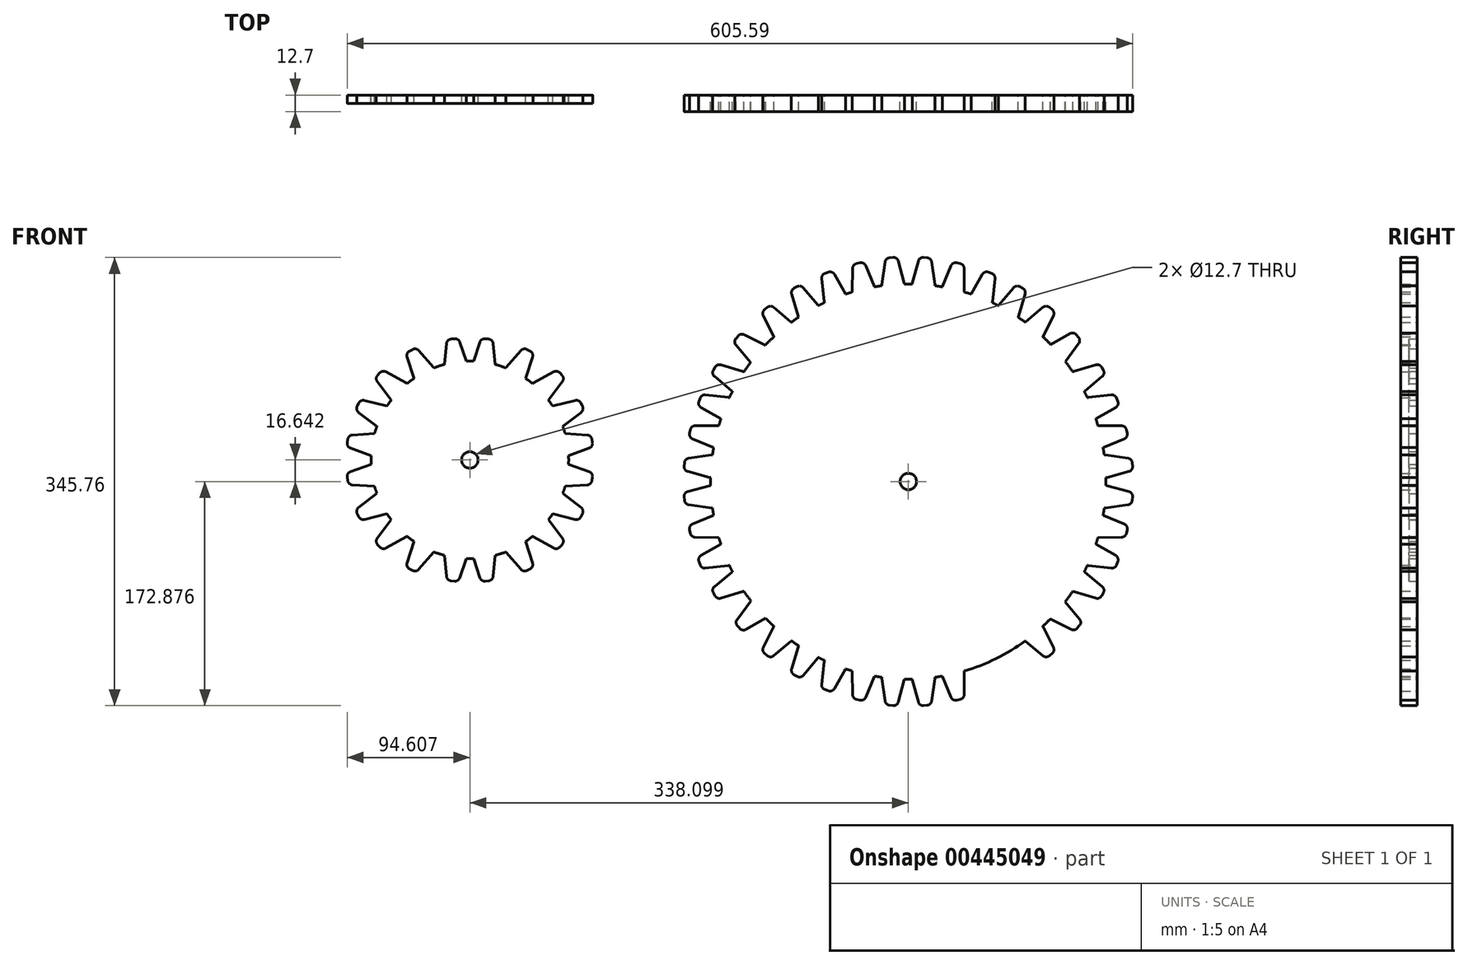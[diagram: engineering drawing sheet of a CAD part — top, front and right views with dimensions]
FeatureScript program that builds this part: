
annotation { "Feature Type Name" : "Feature", "Feature Type Description" : "" }
export const myFeature = defineFeature(function(context is Context, id is Id, definition is map)
    precondition{}
    {
        {
            var Q0;
            Q0=qCreatedBy(makeId("Front.planeOp"),FACE);
            var sketch = newSketch(context, id + "F0", { "sketchPlane" : qUnion([Q0])});
            skCircle(sketch, "E0", {"center": v(90.4, 32.98) * mm, "radius": 152.4 * mm});
            skCircle(sketch, "E1", {"center": v(90.4, 32.98) * mm, "radius": 6.35 * mm});
            skCircle(sketch, "E2", {"center": v(-294.65, -11.85) * mm, "radius": 76.2 * mm});
            skCircle(sketch, "E3", {"center": v(-294.65, -11.85) * mm, "radius": 6.35 * mm});
            skLineSegment(sketch, "E4", {"start": v(-82.46, 44.7) * mm, "end": v(-82.22, 47.48) * mm});
            skLineSegment(sketch, "E5", {"start": v(-78.98, 50.92) * mm, "end": v(-61.5, 53.51) * mm});
            skLineSegment(sketch, "E6", {"start": v(-57.15, 49.41) * mm, "end": v(-58.01, 39.52) * mm});
            skLineSegment(sketch, "E7", {"start": v(-62.8, 36.17) * mm, "end": v(-79.65, 40.7) * mm});
            skPoint(sketch, "E8.visualSharp", {"position": v(-82.74, 41.52) * mm});
            skArc(sketch, "E8.filletArc", {"start": v(-82.46, 44.7) * mm, "mid": v(-81.78, 42.19) * mm, "end": v(-79.65, 40.7) * mm});
            skPoint(sketch, "E9.visualSharp", {"position": v(-81.95, 50.47) * mm});
            skArc(sketch, "E9.filletArc", {"start": v(-78.98, 50.92) * mm, "mid": v(-81.2, 49.76) * mm, "end": v(-82.22, 47.48) * mm});
            skArc(sketch, "E10.filletArc", {"start": v(-57.15, 49.41) * mm, "mid": v(-58.33, 52.52) * mm, "end": v(-61.5, 53.51) * mm});
            skArc(sketch, "E11.filletArc", {"start": v(-62.8, 36.17) * mm, "mid": v(-59.62, 36.73) * mm, "end": v(-58.01, 39.52) * mm});
            skLineSegment(sketch, "E12", {"start": v(-71.1, 94.66) * mm, "end": v(-70.15, 97.29) * mm});
            skLineSegment(sketch, "E13", {"start": v(-66.15, 99.78) * mm, "end": v(-48.58, 97.84) * mm});
            skLineSegment(sketch, "E14", {"start": v(-45.42, 92.76) * mm, "end": v(-48.78, 83.42) * mm});
            skLineSegment(sketch, "E15", {"start": v(-54.25, 81.4) * mm, "end": v(-69.4, 90.07) * mm});
            skPoint(sketch, "E16.visualSharp", {"position": v(-72.18, 91.66) * mm});
            skArc(sketch, "E16.filletArc", {"start": v(-71.1, 94.66) * mm, "mid": v(-71.09, 92.06) * mm, "end": v(-69.4, 90.07) * mm});
            skArc(sketch, "E17.filletArc", {"start": v(-66.15, 99.78) * mm, "mid": v(-68.58, 99.23) * mm, "end": v(-70.15, 97.29) * mm});
            skArc(sketch, "E18.filletArc", {"start": v(-45.42, 92.76) * mm, "mid": v(-45.77, 96.07) * mm, "end": v(-48.58, 97.84) * mm});
            skArc(sketch, "E19.filletArc", {"start": v(-54.25, 81.4) * mm, "mid": v(-51.05, 81.13) * mm, "end": v(-48.78, 83.42) * mm});
            skLineSegment(sketch, "E20", {"start": v(-59.95, 118.83) * mm, "end": v(-58.56, 121.24) * mm});
            skLineSegment(sketch, "E21", {"start": v(-54.17, 122.99) * mm, "end": v(-37.23, 117.95) * mm});
            skLineSegment(sketch, "E22", {"start": v(-35.02, 112.4) * mm, "end": v(-39.98, 103.8) * mm});
            skLineSegment(sketch, "E23", {"start": v(-45.73, 102.79) * mm, "end": v(-59.1, 114) * mm});
            skPoint(sketch, "E24.visualSharp", {"position": v(-61.55, 116.06) * mm});
            skArc(sketch, "E24.filletArc", {"start": v(-59.95, 118.83) * mm, "mid": v(-60.4, 116.26) * mm, "end": v(-59.1, 114) * mm});
            skPoint(sketch, "E25.visualSharp", {"position": v(-57.05, 123.84) * mm});
            skArc(sketch, "E25.filletArc", {"start": v(-54.17, 122.99) * mm, "mid": v(-56.67, 122.88) * mm, "end": v(-58.56, 121.24) * mm});
            skArc(sketch, "E26.filletArc", {"start": v(-35.02, 112.4) * mm, "mid": v(-34.78, 115.71) * mm, "end": v(-37.23, 117.95) * mm});
            skArc(sketch, "E27.filletArc", {"start": v(-45.73, 102.79) * mm, "mid": v(-42.62, 101.95) * mm, "end": v(-39.98, 103.8) * mm});
            skLineSegment(sketch, "E28", {"start": v(-78.33, 70.27) * mm, "end": v(-77.71, 72.99) * mm});
            skLineSegment(sketch, "E29", {"start": v(-74.04, 75.96) * mm, "end": v(-56.37, 76.18) * mm});
            skLineSegment(sketch, "E30", {"start": v(-52.61, 71.53) * mm, "end": v(-54.8, 61.85) * mm});
            skLineSegment(sketch, "E31", {"start": v(-59.99, 59.17) * mm, "end": v(-76.08, 65.92) * mm});
            skPoint(sketch, "E32.visualSharp", {"position": v(-79.03, 67.15) * mm});
            skArc(sketch, "E32.filletArc", {"start": v(-78.33, 70.27) * mm, "mid": v(-78, 67.68) * mm, "end": v(-76.08, 65.92) * mm});
            skPoint(sketch, "E33.visualSharp", {"position": v(-77.05, 75.92) * mm});
            skArc(sketch, "E33.filletArc", {"start": v(-74.04, 75.96) * mm, "mid": v(-76.4, 75.1) * mm, "end": v(-77.71, 72.99) * mm});
            skArc(sketch, "E34.filletArc", {"start": v(-52.61, 71.53) * mm, "mid": v(-53.37, 74.77) * mm, "end": v(-56.37, 76.18) * mm});
            skArc(sketch, "E35.filletArc", {"start": v(-59.99, 59.17) * mm, "mid": v(-56.77, 59.3) * mm, "end": v(-54.8, 61.85) * mm});
            skLineSegment(sketch, "E36.MirrorCS", {"start": v(-7.67, 143.95) * mm, "end": v(-0.07, 150.34) * mm});
            skLineSegment(sketch, "E37.MirrorCS", {"start": v(-0.07, 156.17) * mm, "end": v(-13.44, 167.4) * mm});
            skLineSegment(sketch, "E38.MirrorCS", {"start": v(-21.43, 160.98) * mm, "end": v(-13.53, 145.17) * mm});
            skPoint(sketch, "E39.MirrorP", {"position": v(-22.77, 163.67) * mm});
            skArc(sketch, "E40.MirrorCS", {"start": v(-21.43, 160.98) * mm, "mid": v(-21.75, 163.45) * mm, "end": v(-20.47, 165.6) * mm});
            skArc(sketch, "E41.MirrorCS", {"start": v(-18.33, 167.4) * mm, "mid": v(-15.88, 168.28) * mm, "end": v(-13.44, 167.4) * mm});
            skLineSegment(sketch, "E42.MirrorCS", {"start": v(-18.33, 167.4) * mm, "end": v(-20.47, 165.6) * mm});
            skArc(sketch, "E43.MirrorCS", {"start": v(-7.67, 143.95) * mm, "mid": v(-10.9, 143.14) * mm, "end": v(-13.53, 145.17) * mm});
            skArc(sketch, "E44.MirrorCS", {"start": v(-0.07, 156.17) * mm, "mid": v(1.3, 153.25) * mm, "end": v(-0.07, 150.34) * mm});
            skLineSegment(sketch, "E45.MirrorCS", {"start": v(10.98, 158.4) * mm, "end": v(19.58, 163.36) * mm});
            skArc(sketch, "E46.MirrorCS", {"start": v(10.98, 158.4) * mm, "mid": v(7.67, 158.16) * mm, "end": v(5.43, 160.61) * mm});
            skArc(sketch, "E47.MirrorCS", {"start": v(20.6, 169.11) * mm, "mid": v(21.43, 166) * mm, "end": v(19.58, 163.36) * mm});
            skLineSegment(sketch, "E48.MirrorCS", {"start": v(20.6, 169.11) * mm, "end": v(9.38, 182.48) * mm});
            skLineSegment(sketch, "E49.MirrorCS", {"start": v(0.4, 177.55) * mm, "end": v(5.43, 160.61) * mm});
            skPoint(sketch, "E50.MirrorP", {"position": v(-0.46, 180.43) * mm});
            skArc(sketch, "E51.MirrorCS", {"start": v(0.4, 177.55) * mm, "mid": v(0.5, 180.05) * mm, "end": v(2.14, 181.94) * mm});
            skLineSegment(sketch, "E52.MirrorCS", {"start": v(4.55, 183.33) * mm, "end": v(2.14, 181.94) * mm});
            skArc(sketch, "E53.MirrorCS", {"start": v(4.55, 183.33) * mm, "mid": v(7.12, 183.78) * mm, "end": v(9.38, 182.48) * mm});
            skArc(sketch, "E54.MirrorCS", {"start": v(30.62, 168.8) * mm, "mid": v(27.32, 169.15) * mm, "end": v(25.55, 171.97) * mm});
            skLineSegment(sketch, "E55.MirrorCS", {"start": v(30.62, 168.8) * mm, "end": v(39.96, 172.16) * mm});
            skArc(sketch, "E56.MirrorCS", {"start": v(41.98, 177.64) * mm, "mid": v(42.25, 174.43) * mm, "end": v(39.96, 172.16) * mm});
            skLineSegment(sketch, "E57.MirrorCS", {"start": v(41.98, 177.64) * mm, "end": v(33.31, 192.78) * mm});
            skLineSegment(sketch, "E58.MirrorCS", {"start": v(23.6, 189.53) * mm, "end": v(25.55, 171.97) * mm});
            skArc(sketch, "E59.MirrorCS", {"start": v(23.6, 189.53) * mm, "mid": v(24.15, 191.97) * mm, "end": v(26.1, 193.53) * mm});
            skLineSegment(sketch, "E60.MirrorCS", {"start": v(28.72, 194.48) * mm, "end": v(26.1, 193.53) * mm});
            skArc(sketch, "E61.MirrorCS", {"start": v(28.72, 194.48) * mm, "mid": v(31.32, 194.47) * mm, "end": v(33.31, 192.78) * mm});
            skLineSegment(sketch, "E62.MirrorCS", {"start": v(47.42, 197.43) * mm, "end": v(47.2, 179.76) * mm});
            skArc(sketch, "E63.MirrorCS", {"start": v(47.42, 197.43) * mm, "mid": v(48.27, 199.78) * mm, "end": v(50.4, 201.1) * mm});
            skLineSegment(sketch, "E64.MirrorCS", {"start": v(53.11, 201.7) * mm, "end": v(50.4, 201.1) * mm});
            skArc(sketch, "E65.MirrorCS", {"start": v(53.11, 201.7) * mm, "mid": v(55.7, 201.38) * mm, "end": v(57.47, 199.46) * mm});
            skLineSegment(sketch, "E66.MirrorCS", {"start": v(64.2, 183.37) * mm, "end": v(57.47, 199.46) * mm});
            skArc(sketch, "E67.MirrorCS", {"start": v(64.2, 183.37) * mm, "mid": v(64.08, 180.15) * mm, "end": v(61.53, 178.18) * mm});
            skLineSegment(sketch, "E68.MirrorCS", {"start": v(51.85, 176) * mm, "end": v(61.53, 178.18) * mm});
            skArc(sketch, "E69.MirrorCS", {"start": v(51.85, 176) * mm, "mid": v(48.61, 176.75) * mm, "end": v(47.2, 179.76) * mm});
            skArc(sketch, "E70.MirrorCS", {"start": v(73.97, 180.53) * mm, "mid": v(70.86, 181.71) * mm, "end": v(69.87, 184.88) * mm});
            skLineSegment(sketch, "E71.MirrorCS", {"start": v(73.97, 180.53) * mm, "end": v(83.86, 181.4) * mm});
            skArc(sketch, "E72.MirrorCS", {"start": v(87.2, 186.17) * mm, "mid": v(86.65, 183) * mm, "end": v(83.86, 181.4) * mm});
            skLineSegment(sketch, "E73.MirrorCS", {"start": v(87.2, 186.17) * mm, "end": v(82.69, 203.03) * mm});
            skArc(sketch, "E74.MirrorCS", {"start": v(78.68, 205.84) * mm, "mid": v(81.2, 205.17) * mm, "end": v(82.69, 203.03) * mm});
            skLineSegment(sketch, "E75.MirrorCS", {"start": v(78.68, 205.84) * mm, "end": v(75.9, 205.6) * mm});
            skArc(sketch, "E76.MirrorCS", {"start": v(72.47, 202.36) * mm, "mid": v(73.62, 204.58) * mm, "end": v(75.9, 205.6) * mm});
            skLineSegment(sketch, "E77.MirrorCS", {"start": v(72.47, 202.36) * mm, "end": v(69.87, 184.88) * mm});
            skLineSegment(sketch, "E78.MirrorCS", {"start": v(93.6, 186.17) * mm, "end": v(98.12, 203.03) * mm});
            skLineSegment(sketch, "E79.MirrorCS", {"start": v(108.35, 202.36) * mm, "end": v(110.94, 184.88) * mm});
            skArc(sketch, "E80.MirrorCS", {"start": v(106.84, 180.53) * mm, "mid": v(109.95, 181.71) * mm, "end": v(110.94, 184.88) * mm});
            skLineSegment(sketch, "E81.MirrorCS", {"start": v(106.84, 180.53) * mm, "end": v(96.95, 181.4) * mm});
            skArc(sketch, "E82.MirrorCS", {"start": v(93.6, 186.17) * mm, "mid": v(94.16, 183) * mm, "end": v(96.95, 181.4) * mm});
            skLineSegment(sketch, "E83.MirrorCS", {"start": v(102.13, 205.84) * mm, "end": v(104.9, 205.6) * mm});
            skArc(sketch, "E84.MirrorCS", {"start": v(108.35, 202.36) * mm, "mid": v(107.19, 204.58) * mm, "end": v(104.9, 205.6) * mm});
            skArc(sketch, "E85.MirrorCS", {"start": v(102.13, 205.84) * mm, "mid": v(99.62, 205.17) * mm, "end": v(98.12, 203.03) * mm});
            skArc(sketch, "E86.MirrorCS", {"start": v(127.7, 201.7) * mm, "mid": v(125.11, 201.38) * mm, "end": v(123.35, 199.46) * mm});
            skLineSegment(sketch, "E87.MirrorCS", {"start": v(127.7, 201.7) * mm, "end": v(130.42, 201.1) * mm});
            skArc(sketch, "E88.MirrorCS", {"start": v(133.39, 197.43) * mm, "mid": v(132.54, 199.78) * mm, "end": v(130.42, 201.1) * mm});
            skLineSegment(sketch, "E89.MirrorCS", {"start": v(133.39, 197.43) * mm, "end": v(133.6, 179.76) * mm});
            skArc(sketch, "E90.MirrorCS", {"start": v(128.96, 176) * mm, "mid": v(132.2, 176.75) * mm, "end": v(133.6, 179.76) * mm});
            skLineSegment(sketch, "E91.MirrorCS", {"start": v(128.96, 176) * mm, "end": v(119.28, 178.18) * mm});
            skArc(sketch, "E92.MirrorCS", {"start": v(116.6, 183.37) * mm, "mid": v(116.73, 180.15) * mm, "end": v(119.28, 178.18) * mm});
            skLineSegment(sketch, "E93.MirrorCS", {"start": v(116.6, 183.37) * mm, "end": v(123.35, 199.46) * mm});
            skLineSegment(sketch, "E94.MirrorCS", {"start": v(138.83, 177.64) * mm, "end": v(147.5, 192.78) * mm});
            skArc(sketch, "E95.MirrorCS", {"start": v(152.1, 194.48) * mm, "mid": v(149.49, 194.47) * mm, "end": v(147.5, 192.78) * mm});
            skLineSegment(sketch, "E96.MirrorCS", {"start": v(152.1, 194.48) * mm, "end": v(154.72, 193.53) * mm});
            skArc(sketch, "E97.MirrorCS", {"start": v(157.21, 189.53) * mm, "mid": v(156.66, 191.97) * mm, "end": v(154.72, 193.53) * mm});
            skLineSegment(sketch, "E98.MirrorCS", {"start": v(157.21, 189.53) * mm, "end": v(155.27, 171.97) * mm});
            skArc(sketch, "E99.MirrorCS", {"start": v(150.2, 168.8) * mm, "mid": v(153.5, 169.15) * mm, "end": v(155.27, 171.97) * mm});
            skLineSegment(sketch, "E100.MirrorCS", {"start": v(150.2, 168.8) * mm, "end": v(140.85, 172.16) * mm});
            skArc(sketch, "E101.MirrorCS", {"start": v(138.83, 177.64) * mm, "mid": v(138.56, 174.43) * mm, "end": v(140.85, 172.16) * mm});
            skLineSegment(sketch, "E102.MirrorCS", {"start": v(160.22, 169.11) * mm, "end": v(171.43, 182.48) * mm});
            skArc(sketch, "E103.MirrorCS", {"start": v(176.26, 183.33) * mm, "mid": v(173.7, 183.78) * mm, "end": v(171.43, 182.48) * mm});
            skLineSegment(sketch, "E104.MirrorCS", {"start": v(176.26, 183.33) * mm, "end": v(178.67, 181.94) * mm});
            skArc(sketch, "E105.MirrorCS", {"start": v(180.42, 177.55) * mm, "mid": v(180.3, 180.05) * mm, "end": v(178.67, 181.94) * mm});
            skLineSegment(sketch, "E106.MirrorCS", {"start": v(180.42, 177.55) * mm, "end": v(175.38, 160.61) * mm});
            skArc(sketch, "E107.MirrorCS", {"start": v(169.83, 158.4) * mm, "mid": v(173.14, 158.16) * mm, "end": v(175.38, 160.61) * mm});
            skLineSegment(sketch, "E108.MirrorCS", {"start": v(169.83, 158.4) * mm, "end": v(161.23, 163.36) * mm});
            skArc(sketch, "E109.MirrorCS", {"start": v(160.22, 169.11) * mm, "mid": v(159.38, 166) * mm, "end": v(161.23, 163.36) * mm});
            skArc(sketch, "E110.MirrorCS", {"start": v(180.88, 156.17) * mm, "mid": v(179.52, 153.25) * mm, "end": v(180.88, 150.34) * mm});
            skLineSegment(sketch, "E111.MirrorCS", {"start": v(180.88, 156.17) * mm, "end": v(194.25, 167.4) * mm});
            skArc(sketch, "E112.MirrorCS", {"start": v(199.15, 167.4) * mm, "mid": v(196.7, 168.28) * mm, "end": v(194.25, 167.4) * mm});
            skLineSegment(sketch, "E113.MirrorCS", {"start": v(199.15, 167.4) * mm, "end": v(201.28, 165.6) * mm});
            skArc(sketch, "E114.MirrorCS", {"start": v(202.24, 160.98) * mm, "mid": v(202.56, 163.45) * mm, "end": v(201.28, 165.6) * mm});
            skLineSegment(sketch, "E115.MirrorCS", {"start": v(202.24, 160.98) * mm, "end": v(194.34, 145.17) * mm});
            skArc(sketch, "E116.MirrorCS", {"start": v(188.48, 143.95) * mm, "mid": v(191.7, 143.14) * mm, "end": v(194.34, 145.17) * mm});
            skLineSegment(sketch, "E117.MirrorCS", {"start": v(188.48, 143.95) * mm, "end": v(180.88, 150.34) * mm});
            skLineSegment(sketch, "E118.MirrorCS", {"start": v(234.98, 122.99) * mm, "end": v(218.04, 117.95) * mm});
            skArc(sketch, "E119.MirrorCS", {"start": v(234.98, 122.99) * mm, "mid": v(237.48, 122.88) * mm, "end": v(239.37, 121.24) * mm});
            skLineSegment(sketch, "E120.MirrorCS", {"start": v(240.76, 118.83) * mm, "end": v(239.37, 121.24) * mm});
            skArc(sketch, "E121.MirrorCS", {"start": v(240.76, 118.83) * mm, "mid": v(241.21, 116.26) * mm, "end": v(239.91, 114) * mm});
            skLineSegment(sketch, "E122.MirrorCS", {"start": v(226.54, 102.79) * mm, "end": v(239.91, 114) * mm});
            skArc(sketch, "E123.MirrorCS", {"start": v(226.54, 102.79) * mm, "mid": v(223.43, 101.95) * mm, "end": v(220.8, 103.8) * mm});
            skArc(sketch, "E124.MirrorCS", {"start": v(215.83, 112.4) * mm, "mid": v(215.6, 115.71) * mm, "end": v(218.04, 117.95) * mm});
            skLineSegment(sketch, "E125.MirrorCS", {"start": v(246.96, 99.78) * mm, "end": v(229.4, 97.84) * mm});
            skArc(sketch, "E126.MirrorCS", {"start": v(246.96, 99.78) * mm, "mid": v(249.4, 99.23) * mm, "end": v(250.96, 97.29) * mm});
            skLineSegment(sketch, "E127.MirrorCS", {"start": v(251.9, 94.66) * mm, "end": v(250.96, 97.29) * mm});
            skPoint(sketch, "E128.MirrorP", {"position": v(252.99, 91.66) * mm});
            skArc(sketch, "E129.MirrorCS", {"start": v(251.9, 94.66) * mm, "mid": v(251.9, 92.06) * mm, "end": v(250.21, 90.07) * mm});
            skLineSegment(sketch, "E130.MirrorCS", {"start": v(235.07, 81.4) * mm, "end": v(250.21, 90.07) * mm});
            skArc(sketch, "E131.MirrorCS", {"start": v(235.07, 81.4) * mm, "mid": v(231.86, 81.13) * mm, "end": v(229.59, 83.42) * mm});
            skLineSegment(sketch, "E132.MirrorCS", {"start": v(226.23, 92.76) * mm, "end": v(229.59, 83.42) * mm});
            skArc(sketch, "E133.MirrorCS", {"start": v(226.23, 92.76) * mm, "mid": v(226.58, 96.07) * mm, "end": v(229.4, 97.84) * mm});
            skArc(sketch, "E134.MirrorCS", {"start": v(233.42, 71.53) * mm, "mid": v(234.18, 74.77) * mm, "end": v(237.19, 76.18) * mm});
            skLineSegment(sketch, "E135.MirrorCS", {"start": v(254.86, 75.96) * mm, "end": v(237.19, 76.18) * mm});
            skArc(sketch, "E136.MirrorCS", {"start": v(254.86, 75.96) * mm, "mid": v(257.2, 75.1) * mm, "end": v(258.52, 72.99) * mm});
            skLineSegment(sketch, "E137.MirrorCS", {"start": v(259.14, 70.27) * mm, "end": v(258.52, 72.99) * mm});
            skArc(sketch, "E138.MirrorCS", {"start": v(259.14, 70.27) * mm, "mid": v(258.8, 67.68) * mm, "end": v(256.9, 65.92) * mm});
            skLineSegment(sketch, "E139.MirrorCS", {"start": v(240.8, 59.17) * mm, "end": v(256.9, 65.92) * mm});
            skArc(sketch, "E140.MirrorCS", {"start": v(240.8, 59.17) * mm, "mid": v(237.58, 59.3) * mm, "end": v(235.6, 61.85) * mm});
            skLineSegment(sketch, "E141.MirrorCS", {"start": v(233.42, 71.53) * mm, "end": v(235.6, 61.85) * mm});
            skArc(sketch, "E142.MirrorCS", {"start": v(237.96, 49.41) * mm, "mid": v(239.14, 52.52) * mm, "end": v(242.31, 53.51) * mm});
            skLineSegment(sketch, "E143.MirrorCS", {"start": v(259.8, 50.92) * mm, "end": v(242.31, 53.51) * mm});
            skArc(sketch, "E144.MirrorCS", {"start": v(259.8, 50.92) * mm, "mid": v(262, 49.76) * mm, "end": v(263.03, 47.48) * mm});
            skLineSegment(sketch, "E145.MirrorCS", {"start": v(263.27, 44.7) * mm, "end": v(263.03, 47.48) * mm});
            skArc(sketch, "E146.MirrorCS", {"start": v(263.27, 44.7) * mm, "mid": v(262.6, 42.19) * mm, "end": v(260.46, 40.7) * mm});
            skLineSegment(sketch, "E147.MirrorCS", {"start": v(243.6, 36.17) * mm, "end": v(260.46, 40.7) * mm});
            skArc(sketch, "E148.MirrorCS", {"start": v(243.6, 36.17) * mm, "mid": v(240.43, 36.73) * mm, "end": v(238.82, 39.52) * mm});
            skLineSegment(sketch, "E149.MirrorCS", {"start": v(237.96, 49.41) * mm, "end": v(238.82, 39.52) * mm});
            skArc(sketch, "E150.MirrorCS", {"start": v(-62.8, 29.78) * mm, "mid": v(-59.62, 29.22) * mm, "end": v(-58.01, 26.43) * mm});
            skLineSegment(sketch, "E151.MirrorCS", {"start": v(-57.15, 16.54) * mm, "end": v(-58.01, 26.43) * mm});
            skArc(sketch, "E152.MirrorCS", {"start": v(-57.15, 16.54) * mm, "mid": v(-58.33, 13.43) * mm, "end": v(-61.5, 12.44) * mm});
            skLineSegment(sketch, "E153.MirrorCS", {"start": v(-78.98, 15.04) * mm, "end": v(-61.5, 12.44) * mm});
            skPoint(sketch, "E154.MirrorP", {"position": v(-81.95, 15.48) * mm});
            skLineSegment(sketch, "E155.MirrorCS", {"start": v(-82.46, 21.25) * mm, "end": v(-82.22, 18.47) * mm});
            skPoint(sketch, "E156.MirrorP", {"position": v(-82.74, 24.43) * mm});
            skLineSegment(sketch, "E157.MirrorCS", {"start": v(-62.8, 29.78) * mm, "end": v(-79.65, 25.26) * mm});
            skArc(sketch, "E158.MirrorCS", {"start": v(-78.98, 15.04) * mm, "mid": v(-81.2, 16.2) * mm, "end": v(-82.22, 18.47) * mm});
            skArc(sketch, "E159.MirrorCS", {"start": v(-82.46, 21.25) * mm, "mid": v(-81.78, 23.77) * mm, "end": v(-79.65, 25.26) * mm});
            skLineSegment(sketch, "E160.MirrorCS", {"start": v(-59.99, 6.78) * mm, "end": v(-76.08, 0.04) * mm});
            skPoint(sketch, "E161.MirrorP", {"position": v(-79.03, -1.2) * mm});
            skArc(sketch, "E162.MirrorCS", {"start": v(-78.33, -4.32) * mm, "mid": v(-78, -1.73) * mm, "end": v(-76.08, 0.04) * mm});
            skLineSegment(sketch, "E163.MirrorCS", {"start": v(-78.33, -4.32) * mm, "end": v(-77.71, -7.04) * mm});
            skArc(sketch, "E164.MirrorCS", {"start": v(-74.04, -10) * mm, "mid": v(-76.4, -9.16) * mm, "end": v(-77.71, -7.04) * mm});
            skLineSegment(sketch, "E165.MirrorCS", {"start": v(-74.04, -10) * mm, "end": v(-56.37, -10.23) * mm});
            skArc(sketch, "E166.MirrorCS", {"start": v(-52.61, -5.58) * mm, "mid": v(-53.37, -8.82) * mm, "end": v(-56.37, -10.23) * mm});
            skLineSegment(sketch, "E167.MirrorCS", {"start": v(-52.61, -5.58) * mm, "end": v(-54.8, 4.1) * mm});
            skArc(sketch, "E168.MirrorCS", {"start": v(-59.99, 6.78) * mm, "mid": v(-56.77, 6.65) * mm, "end": v(-54.8, 4.1) * mm});
            skArc(sketch, "E169.MirrorCS", {"start": v(-54.25, -15.45) * mm, "mid": v(-51.05, -15.18) * mm, "end": v(-48.78, -17.47) * mm});
            skLineSegment(sketch, "E170.MirrorCS", {"start": v(-45.42, -26.8) * mm, "end": v(-48.78, -17.47) * mm});
            skArc(sketch, "E171.MirrorCS", {"start": v(-45.42, -26.8) * mm, "mid": v(-45.77, -30.11) * mm, "end": v(-48.58, -31.88) * mm});
            skLineSegment(sketch, "E172.MirrorCS", {"start": v(-66.15, -33.83) * mm, "end": v(-48.58, -31.88) * mm});
            skPoint(sketch, "E173.MirrorP", {"position": v(-69.14, -34.16) * mm});
            skArc(sketch, "E174.MirrorCS", {"start": v(-66.15, -33.83) * mm, "mid": v(-68.58, -33.28) * mm, "end": v(-70.15, -31.33) * mm});
            skLineSegment(sketch, "E175.MirrorCS", {"start": v(-71.1, -28.71) * mm, "end": v(-70.15, -31.33) * mm});
            skPoint(sketch, "E176.MirrorP", {"position": v(-72.18, -25.7) * mm});
            skLineSegment(sketch, "E177.MirrorCS", {"start": v(-54.25, -15.45) * mm, "end": v(-69.4, -24.12) * mm});
            skArc(sketch, "E178.MirrorCS", {"start": v(-45.73, -36.84) * mm, "mid": v(-42.62, -36) * mm, "end": v(-39.98, -37.85) * mm});
            skArc(sketch, "E179.MirrorCS", {"start": v(-35.02, -46.45) * mm, "mid": v(-34.78, -49.76) * mm, "end": v(-37.23, -52) * mm});
            skLineSegment(sketch, "E180.MirrorCS", {"start": v(-54.17, -57.04) * mm, "end": v(-37.23, -52) * mm});
            skLineSegment(sketch, "E181.MirrorCS", {"start": v(-45.73, -36.84) * mm, "end": v(-59.1, -48.05) * mm});
            skArc(sketch, "E182.MirrorCS", {"start": v(-59.95, -52.88) * mm, "mid": v(-60.4, -50.31) * mm, "end": v(-59.1, -48.05) * mm});
            skLineSegment(sketch, "E183.MirrorCS", {"start": v(-59.95, -52.88) * mm, "end": v(-58.56, -55.29) * mm});
            skArc(sketch, "E184.MirrorCS", {"start": v(-54.17, -57.04) * mm, "mid": v(-56.67, -56.92) * mm, "end": v(-58.56, -55.29) * mm});
            skArc(sketch, "E185.MirrorCS", {"start": v(-7.67, -78) * mm, "mid": v(-10.9, -77.2) * mm, "end": v(-13.53, -79.22) * mm});
            skLineSegment(sketch, "E186.MirrorCS", {"start": v(-7.67, -78) * mm, "end": v(-0.07, -84.38) * mm});
            skArc(sketch, "E187.MirrorCS", {"start": v(-0.07, -90.22) * mm, "mid": v(1.3, -87.3) * mm, "end": v(-0.07, -84.38) * mm});
            skLineSegment(sketch, "E188.MirrorCS", {"start": v(-0.07, -90.22) * mm, "end": v(-13.44, -101.44) * mm});
            skArc(sketch, "E189.MirrorCS", {"start": v(-71.1, -28.71) * mm, "mid": v(-71.09, -26.1) * mm, "end": v(-69.4, -24.12) * mm});
            skLineSegment(sketch, "E190.MirrorCS", {"start": v(-35.02, -46.45) * mm, "end": v(-39.98, -37.85) * mm});
            skArc(sketch, "E191.MirrorCS", {"start": v(-18.33, -101.44) * mm, "mid": v(-15.88, -102.33) * mm, "end": v(-13.44, -101.44) * mm});
            skLineSegment(sketch, "E192.MirrorCS", {"start": v(-18.33, -101.44) * mm, "end": v(-20.47, -99.65) * mm});
            skArc(sketch, "E193.MirrorCS", {"start": v(-21.43, -95.03) * mm, "mid": v(-21.75, -97.5) * mm, "end": v(-20.47, -99.65) * mm});
            skLineSegment(sketch, "E194.MirrorCS", {"start": v(-21.43, -95.03) * mm, "end": v(-13.53, -79.22) * mm});
            skArc(sketch, "E195.MirrorCS", {"start": v(10.98, -92.45) * mm, "mid": v(7.67, -92.2) * mm, "end": v(5.43, -94.66) * mm});
            skLineSegment(sketch, "E196.MirrorCS", {"start": v(0.4, -111.6) * mm, "end": v(5.43, -94.66) * mm});
            skArc(sketch, "E197.MirrorCS", {"start": v(0.4, -111.6) * mm, "mid": v(0.5, -114.1) * mm, "end": v(2.14, -115.99) * mm});
            skLineSegment(sketch, "E198.MirrorCS", {"start": v(4.55, -117.38) * mm, "end": v(2.14, -115.99) * mm});
            skArc(sketch, "E199.MirrorCS", {"start": v(4.55, -117.38) * mm, "mid": v(7.12, -117.83) * mm, "end": v(9.38, -116.53) * mm});
            skLineSegment(sketch, "E200.MirrorCS", {"start": v(20.6, -103.16) * mm, "end": v(9.38, -116.53) * mm});
            skArc(sketch, "E201.MirrorCS", {"start": v(20.6, -103.16) * mm, "mid": v(21.43, -100.05) * mm, "end": v(19.58, -97.41) * mm});
            skLineSegment(sketch, "E202.MirrorCS", {"start": v(10.98, -92.45) * mm, "end": v(19.58, -97.41) * mm});
            skArc(sketch, "E203.MirrorCS", {"start": v(30.62, -102.85) * mm, "mid": v(27.32, -103.2) * mm, "end": v(25.55, -106.01) * mm});
            skLineSegment(sketch, "E204.MirrorCS", {"start": v(30.62, -102.85) * mm, "end": v(39.96, -106.2) * mm});
            skArc(sketch, "E205.MirrorCS", {"start": v(41.98, -111.68) * mm, "mid": v(42.25, -108.48) * mm, "end": v(39.96, -106.2) * mm});
            skLineSegment(sketch, "E206.MirrorCS", {"start": v(41.98, -111.68) * mm, "end": v(33.31, -126.83) * mm});
            skArc(sketch, "E207.MirrorCS", {"start": v(28.72, -128.53) * mm, "mid": v(31.32, -128.52) * mm, "end": v(33.31, -126.83) * mm});
            skLineSegment(sketch, "E208.MirrorCS", {"start": v(28.72, -128.53) * mm, "end": v(26.1, -127.58) * mm});
            skArc(sketch, "E209.MirrorCS", {"start": v(23.6, -123.58) * mm, "mid": v(24.15, -126.01) * mm, "end": v(26.1, -127.58) * mm});
            skLineSegment(sketch, "E210.MirrorCS", {"start": v(23.6, -123.58) * mm, "end": v(25.55, -106.01) * mm});
            skLineSegment(sketch, "E211.MirrorCS", {"start": v(47.42, -131.47) * mm, "end": v(47.2, -113.8) * mm});
            skArc(sketch, "E212.MirrorCS", {"start": v(51.85, -110.04) * mm, "mid": v(48.61, -110.8) * mm, "end": v(47.2, -113.8) * mm});
            skLineSegment(sketch, "E213.MirrorCS", {"start": v(51.85, -110.04) * mm, "end": v(61.53, -112.23) * mm});
            skArc(sketch, "E214.MirrorCS", {"start": v(64.2, -117.42) * mm, "mid": v(64.08, -114.2) * mm, "end": v(61.53, -112.23) * mm});
            skLineSegment(sketch, "E215.MirrorCS", {"start": v(64.2, -117.42) * mm, "end": v(57.47, -133.51) * mm});
            skArc(sketch, "E216.MirrorCS", {"start": v(53.11, -135.76) * mm, "mid": v(55.7, -135.43) * mm, "end": v(57.47, -133.51) * mm});
            skLineSegment(sketch, "E217.MirrorCS", {"start": v(53.11, -135.76) * mm, "end": v(50.4, -135.14) * mm});
            skArc(sketch, "E218.MirrorCS", {"start": v(47.42, -131.47) * mm, "mid": v(48.27, -133.82) * mm, "end": v(50.4, -135.14) * mm});
            skLineSegment(sketch, "E219.MirrorCS", {"start": v(72.47, -136.41) * mm, "end": v(69.87, -118.93) * mm});
            skArc(sketch, "E220.MirrorCS", {"start": v(73.97, -114.58) * mm, "mid": v(70.86, -115.76) * mm, "end": v(69.87, -118.93) * mm});
            skLineSegment(sketch, "E221.MirrorCS", {"start": v(73.97, -114.58) * mm, "end": v(83.86, -115.44) * mm});
            skArc(sketch, "E222.MirrorCS", {"start": v(87.2, -120.22) * mm, "mid": v(86.65, -117.05) * mm, "end": v(83.86, -115.44) * mm});
            skLineSegment(sketch, "E223.MirrorCS", {"start": v(87.2, -120.22) * mm, "end": v(82.69, -137.08) * mm});
            skArc(sketch, "E224.MirrorCS", {"start": v(78.68, -139.89) * mm, "mid": v(81.2, -139.21) * mm, "end": v(82.69, -137.08) * mm});
            skLineSegment(sketch, "E225.MirrorCS", {"start": v(78.68, -139.89) * mm, "end": v(75.9, -139.65) * mm});
            skArc(sketch, "E226.MirrorCS", {"start": v(72.47, -136.41) * mm, "mid": v(73.62, -138.62) * mm, "end": v(75.9, -139.65) * mm});
            skLineSegment(sketch, "E227.MirrorCS", {"start": v(93.6, -120.22) * mm, "end": v(98.12, -137.08) * mm});
            skArc(sketch, "E228.MirrorCS", {"start": v(93.6, -120.22) * mm, "mid": v(94.16, -117.05) * mm, "end": v(96.95, -115.44) * mm});
            skLineSegment(sketch, "E229.MirrorCS", {"start": v(106.84, -114.58) * mm, "end": v(96.95, -115.44) * mm});
            skArc(sketch, "E230.MirrorCS", {"start": v(106.84, -114.58) * mm, "mid": v(109.95, -115.76) * mm, "end": v(110.94, -118.93) * mm});
            skLineSegment(sketch, "E231.MirrorCS", {"start": v(108.35, -136.41) * mm, "end": v(110.94, -118.93) * mm});
            skArc(sketch, "E232.MirrorCS", {"start": v(108.35, -136.41) * mm, "mid": v(107.19, -138.62) * mm, "end": v(104.9, -139.65) * mm});
            skLineSegment(sketch, "E233.MirrorCS", {"start": v(102.13, -139.89) * mm, "end": v(104.9, -139.65) * mm});
            skArc(sketch, "E234.MirrorCS", {"start": v(102.13, -139.89) * mm, "mid": v(99.62, -139.21) * mm, "end": v(98.12, -137.08) * mm});
            skArc(sketch, "E235.MirrorCS", {"start": v(127.7, -135.76) * mm, "mid": v(125.11, -135.43) * mm, "end": v(123.35, -133.51) * mm});
            skLineSegment(sketch, "E236.MirrorCS", {"start": v(127.7, -135.76) * mm, "end": v(130.42, -135.14) * mm});
            skArc(sketch, "E237.MirrorCS", {"start": v(133.39, -131.47) * mm, "mid": v(132.54, -133.82) * mm, "end": v(130.42, -135.14) * mm});
            skLineSegment(sketch, "E238.MirrorCS", {"start": v(133.39, -131.47) * mm, "end": v(133.6, -113.8) * mm});
            skArc(sketch, "E239.MirrorCS", {"start": v(128.96, -110.04) * mm, "mid": v(132.2, -110.8) * mm, "end": v(133.6, -113.8) * mm});
            skLineSegment(sketch, "E240.MirrorCS", {"start": v(128.96, -110.04) * mm, "end": v(119.28, -112.23) * mm});
            skArc(sketch, "E241.MirrorCS", {"start": v(116.6, -117.42) * mm, "mid": v(116.73, -114.2) * mm, "end": v(119.28, -112.23) * mm});
            skLineSegment(sketch, "E242.MirrorCS", {"start": v(116.6, -117.42) * mm, "end": v(123.35, -133.51) * mm});
            skLineSegment(sketch, "E243.MirrorCS", {"start": v(152.1, -128.53) * mm, "end": v(154.72, -127.58) * mm});
            skArc(sketch, "E244.MirrorCS", {"start": v(157.21, -123.58) * mm, "mid": v(156.66, -126.01) * mm, "end": v(154.72, -127.58) * mm});
            skArc(sketch, "E245.MirrorCS", {"start": v(150.2, -102.85) * mm, "mid": v(153.5, -103.2) * mm, "end": v(155.27, -106.01) * mm});
            skArc(sketch, "E246.MirrorCS", {"start": v(138.83, -111.68) * mm, "mid": v(138.56, -108.48) * mm, "end": v(140.85, -106.2) * mm});
            skLineSegment(sketch, "E247.MirrorCS", {"start": v(138.83, -111.68) * mm, "end": v(147.5, -126.83) * mm});
            skArc(sketch, "E248.MirrorCS", {"start": v(152.1, -128.53) * mm, "mid": v(149.49, -128.52) * mm, "end": v(147.5, -126.83) * mm});
            skLineSegment(sketch, "E249.MirrorCS", {"start": v(160.22, -103.16) * mm, "end": v(171.43, -116.53) * mm});
            skArc(sketch, "E250.MirrorCS", {"start": v(176.26, -117.38) * mm, "mid": v(173.7, -117.83) * mm, "end": v(171.43, -116.53) * mm});
            skLineSegment(sketch, "E251.MirrorCS", {"start": v(176.26, -117.38) * mm, "end": v(178.67, -115.99) * mm});
            skArc(sketch, "E252.MirrorCS", {"start": v(180.42, -111.6) * mm, "mid": v(180.3, -114.1) * mm, "end": v(178.67, -115.99) * mm});
            skLineSegment(sketch, "E253.MirrorCS", {"start": v(180.42, -111.6) * mm, "end": v(175.38, -94.66) * mm});
            skArc(sketch, "E254.MirrorCS", {"start": v(169.83, -92.45) * mm, "mid": v(173.14, -92.2) * mm, "end": v(175.38, -94.66) * mm});
            skArc(sketch, "E255.MirrorCS", {"start": v(160.22, -103.16) * mm, "mid": v(159.38, -100.05) * mm, "end": v(161.23, -97.41) * mm});
            skLineSegment(sketch, "E256.MirrorCS", {"start": v(180.88, -90.22) * mm, "end": v(194.25, -101.44) * mm});
            skArc(sketch, "E257.MirrorCS", {"start": v(180.88, -90.22) * mm, "mid": v(179.52, -87.3) * mm, "end": v(180.88, -84.38) * mm});
            skLineSegment(sketch, "E258.MirrorCS", {"start": v(188.48, -78) * mm, "end": v(180.88, -84.38) * mm});
            skArc(sketch, "E259.MirrorCS", {"start": v(188.48, -78) * mm, "mid": v(191.7, -77.2) * mm, "end": v(194.34, -79.22) * mm});
            skLineSegment(sketch, "E260.MirrorCS", {"start": v(202.24, -95.03) * mm, "end": v(194.34, -79.22) * mm});
            skArc(sketch, "E261.MirrorCS", {"start": v(199.15, -101.44) * mm, "mid": v(196.7, -102.33) * mm, "end": v(194.25, -101.44) * mm});
            skLineSegment(sketch, "E262.MirrorCS", {"start": v(234.98, -57.04) * mm, "end": v(218.04, -52) * mm});
            skArc(sketch, "E263.MirrorCS", {"start": v(234.98, -57.04) * mm, "mid": v(237.48, -56.92) * mm, "end": v(239.37, -55.29) * mm});
            skLineSegment(sketch, "E264.MirrorCS", {"start": v(240.76, -52.88) * mm, "end": v(239.37, -55.29) * mm});
            skLineSegment(sketch, "E265.MirrorCS", {"start": v(226.54, -36.84) * mm, "end": v(239.91, -48.05) * mm});
            skArc(sketch, "E266.MirrorCS", {"start": v(226.54, -36.84) * mm, "mid": v(223.43, -36) * mm, "end": v(220.8, -37.85) * mm});
            skLineSegment(sketch, "E267.MirrorCS", {"start": v(215.83, -46.45) * mm, "end": v(220.8, -37.85) * mm});
            skArc(sketch, "E268.MirrorCS", {"start": v(215.83, -46.45) * mm, "mid": v(215.6, -49.76) * mm, "end": v(218.04, -52) * mm});
            skLineSegment(sketch, "E269.MirrorCS", {"start": v(246.96, -33.83) * mm, "end": v(229.4, -31.88) * mm});
            skArc(sketch, "E270.MirrorCS", {"start": v(226.23, -26.8) * mm, "mid": v(226.58, -30.11) * mm, "end": v(229.4, -31.88) * mm});
            skLineSegment(sketch, "E271.MirrorCS", {"start": v(226.23, -26.8) * mm, "end": v(229.59, -17.47) * mm});
            skArc(sketch, "E272.MirrorCS", {"start": v(235.07, -15.45) * mm, "mid": v(231.86, -15.18) * mm, "end": v(229.59, -17.47) * mm});
            skLineSegment(sketch, "E273.MirrorCS", {"start": v(235.07, -15.45) * mm, "end": v(250.21, -24.12) * mm});
            skArc(sketch, "E274.MirrorCS", {"start": v(251.9, -28.71) * mm, "mid": v(251.9, -26.1) * mm, "end": v(250.21, -24.12) * mm});
            skLineSegment(sketch, "E275.MirrorCS", {"start": v(251.9, -28.71) * mm, "end": v(250.96, -31.33) * mm});
            skPoint(sketch, "E276.MirrorP", {"position": v(249.95, -34.16) * mm});
            skArc(sketch, "E277.MirrorCS", {"start": v(246.96, -33.83) * mm, "mid": v(249.4, -33.28) * mm, "end": v(250.96, -31.33) * mm});
            skLineSegment(sketch, "E278.MirrorCS", {"start": v(254.86, -10) * mm, "end": v(237.19, -10.23) * mm});
            skArc(sketch, "E279.MirrorCS", {"start": v(233.42, -5.58) * mm, "mid": v(234.18, -8.82) * mm, "end": v(237.19, -10.23) * mm});
            skLineSegment(sketch, "E280.MirrorCS", {"start": v(240.8, 6.78) * mm, "end": v(256.9, 0.04) * mm});
            skArc(sketch, "E281.MirrorCS", {"start": v(259.14, -4.32) * mm, "mid": v(258.8, -1.73) * mm, "end": v(256.9, 0.04) * mm});
            skLineSegment(sketch, "E282.MirrorCS", {"start": v(259.14, -4.32) * mm, "end": v(258.52, -7.04) * mm});
            skLineSegment(sketch, "E283.MirrorCS", {"start": v(259.8, 15.04) * mm, "end": v(242.31, 12.44) * mm});
            skLineSegment(sketch, "E284.MirrorCS", {"start": v(237.96, 16.54) * mm, "end": v(238.82, 26.43) * mm});
            skArc(sketch, "E285.MirrorCS", {"start": v(243.6, 29.78) * mm, "mid": v(240.43, 29.22) * mm, "end": v(238.82, 26.43) * mm});
            skLineSegment(sketch, "E286.MirrorCS", {"start": v(243.6, 29.78) * mm, "end": v(260.46, 25.26) * mm});
            skArc(sketch, "E287.MirrorCS", {"start": v(263.27, 21.25) * mm, "mid": v(262.6, 23.77) * mm, "end": v(260.46, 25.26) * mm});
            skLineSegment(sketch, "E288.MirrorCS", {"start": v(263.27, 21.25) * mm, "end": v(263.03, 18.47) * mm});
            skArc(sketch, "E289.MirrorCS", {"start": v(259.8, 15.04) * mm, "mid": v(262, 16.2) * mm, "end": v(263.03, 18.47) * mm});
            skLineSegment(sketch, "E290.MirrorCS", {"start": v(150.2, -102.85) * mm, "end": v(140.85, -106.2) * mm});
            skLineSegment(sketch, "E291.MirrorCS", {"start": v(169.83, -92.45) * mm, "end": v(161.23, -97.41) * mm});
            skLineSegment(sketch, "E292.MirrorCS", {"start": v(157.21, -123.58) * mm, "end": v(155.27, -106.01) * mm});
            skArc(sketch, "E293.MirrorCS", {"start": v(202.24, -95.03) * mm, "mid": v(202.56, -97.5) * mm, "end": v(201.28, -99.65) * mm});
            skLineSegment(sketch, "E294.MirrorCS", {"start": v(199.15, -101.44) * mm, "end": v(201.28, -99.65) * mm});
            skArc(sketch, "E295.MirrorCS", {"start": v(240.76, -52.88) * mm, "mid": v(241.21, -50.31) * mm, "end": v(239.91, -48.05) * mm});
            skArc(sketch, "E296.MirrorCS", {"start": v(237.96, 16.54) * mm, "mid": v(239.14, 13.43) * mm, "end": v(242.31, 12.44) * mm});
            skArc(sketch, "E297.MirrorCS", {"start": v(254.86, -10) * mm, "mid": v(257.2, -9.16) * mm, "end": v(258.52, -7.04) * mm});
            skLineSegment(sketch, "E298.MirrorCS", {"start": v(233.42, -5.58) * mm, "end": v(235.6, 4.1) * mm});
            skArc(sketch, "E299.MirrorCS", {"start": v(240.8, 6.78) * mm, "mid": v(237.58, 6.65) * mm, "end": v(235.6, 4.1) * mm});
            skLineSegment(sketch, "E300", {"start": v(-389.2, 1.52) * mm, "end": v(-388.72, 4.27) * mm});
            skLineSegment(sketch, "E301", {"start": v(-385.2, 7.41) * mm, "end": v(-367.55, 8.47) * mm});
            skLineSegment(sketch, "E302", {"start": v(-363.57, 4) * mm, "end": v(-365.3, -5.77) * mm});
            skLineSegment(sketch, "E303", {"start": v(-370.35, -8.69) * mm, "end": v(-386.75, -2.72) * mm});
            skPoint(sketch, "E304.visualSharp", {"position": v(-389.75, -1.62) * mm});
            skArc(sketch, "E304.filletArc", {"start": v(-389.2, 1.52) * mm, "mid": v(-388.75, -1.04) * mm, "end": v(-386.75, -2.72) * mm});
            skPoint(sketch, "E305.visualSharp", {"position": v(-388.2, 7.23) * mm});
            skArc(sketch, "E305.filletArc", {"start": v(-385.2, 7.41) * mm, "mid": v(-387.5, 6.45) * mm, "end": v(-388.72, 4.27) * mm});
            skArc(sketch, "E306.filletArc", {"start": v(-363.57, 4) * mm, "mid": v(-364.48, 7.2) * mm, "end": v(-367.55, 8.47) * mm});
            skArc(sketch, "E307.filletArc", {"start": v(-370.35, -8.69) * mm, "mid": v(-367.14, -8.4) * mm, "end": v(-365.3, -5.77) * mm});
            skLineSegment(sketch, "E308", {"start": v(-309.16, 81.42) * mm, "end": v(-306.39, 81.66) * mm});
            skLineSegment(sketch, "E309", {"start": v(-302.44, 79.07) * mm, "end": v(-296.85, 62.3) * mm});
            skLineSegment(sketch, "E310", {"start": v(-300.13, 57.3) * mm, "end": v(-310.02, 56.44) * mm});
            skLineSegment(sketch, "E311", {"start": v(-314.15, 60.57) * mm, "end": v(-312.63, 77.95) * mm});
            skPoint(sketch, "E312.visualSharp", {"position": v(-312.35, 81.14) * mm});
            skArc(sketch, "E312.filletArc", {"start": v(-309.16, 81.42) * mm, "mid": v(-311.53, 80.32) * mm, "end": v(-312.63, 77.95) * mm});
            skPoint(sketch, "E313.visualSharp", {"position": v(-303.4, 81.92) * mm});
            skArc(sketch, "E313.filletArc", {"start": v(-302.44, 79.07) * mm, "mid": v(-303.97, 81.05) * mm, "end": v(-306.39, 81.66) * mm});
            skArc(sketch, "E314.filletArc", {"start": v(-300.13, 57.3) * mm, "mid": v(-297.28, 59.01) * mm, "end": v(-296.85, 62.3) * mm});
            skArc(sketch, "E315.filletArc", {"start": v(-314.15, 60.57) * mm, "mid": v(-313.05, 57.54) * mm, "end": v(-310.02, 56.44) * mm});
            skLineSegment(sketch, "E316", {"start": v(-365.77, 53.37) * mm, "end": v(-363.88, 55.42) * mm});
            skLineSegment(sketch, "E317", {"start": v(-359.22, 56.15) * mm, "end": v(-343.81, 47.5) * mm});
            skLineSegment(sketch, "E318", {"start": v(-342.88, 41.59) * mm, "end": v(-349.62, 34.3) * mm});
            skLineSegment(sketch, "E319", {"start": v(-355.45, 34.58) * mm, "end": v(-366, 48.48) * mm});
            skPoint(sketch, "E320.visualSharp", {"position": v(-367.94, 51.03) * mm});
            skArc(sketch, "E320.filletArc", {"start": v(-365.77, 53.37) * mm, "mid": v(-366.78, 50.97) * mm, "end": v(-366, 48.48) * mm});
            skPoint(sketch, "E321.visualSharp", {"position": v(-361.84, 57.63) * mm});
            skArc(sketch, "E321.filletArc", {"start": v(-359.22, 56.15) * mm, "mid": v(-361.68, 56.6) * mm, "end": v(-363.88, 55.42) * mm});
            skArc(sketch, "E322.filletArc", {"start": v(-342.88, 41.59) * mm, "mid": v(-341.91, 44.77) * mm, "end": v(-343.81, 47.5) * mm});
            skArc(sketch, "E323.filletArc", {"start": v(-355.45, 34.58) * mm, "mid": v(-352.6, 33.08) * mm, "end": v(-349.62, 34.3) * mm});
            skLineSegment(sketch, "E324", {"start": v(-341.2, 72.18) * mm, "end": v(-338.73, 73.47) * mm});
            skLineSegment(sketch, "E325", {"start": v(-334.09, 72.6) * mm, "end": v(-322.47, 59.3) * mm});
            skLineSegment(sketch, "E326", {"start": v(-323.57, 53.42) * mm, "end": v(-332.36, 48.8) * mm});
            skLineSegment(sketch, "E327", {"start": v(-337.76, 51.02) * mm, "end": v(-343.06, 67.65) * mm});
            skPoint(sketch, "E328.visualSharp", {"position": v(-344.03, 70.7) * mm});
            skArc(sketch, "E328.filletArc", {"start": v(-341.2, 72.18) * mm, "mid": v(-342.95, 70.25) * mm, "end": v(-343.06, 67.65) * mm});
            skPoint(sketch, "E329.visualSharp", {"position": v(-336.07, 74.87) * mm});
            skArc(sketch, "E329.filletArc", {"start": v(-334.09, 72.6) * mm, "mid": v(-336.26, 73.85) * mm, "end": v(-338.73, 73.47) * mm});
            skArc(sketch, "E330.filletArc", {"start": v(-323.57, 53.42) * mm, "mid": v(-321.6, 56.09) * mm, "end": v(-322.47, 59.3) * mm});
            skArc(sketch, "E331.filletArc", {"start": v(-337.76, 51.02) * mm, "mid": v(-335.57, 48.65) * mm, "end": v(-332.36, 48.8) * mm});
            skLineSegment(sketch, "E332", {"start": v(-381.48, 29.67) * mm, "end": v(-380.2, 32.14) * mm});
            skLineSegment(sketch, "E333", {"start": v(-375.89, 34.07) * mm, "end": v(-358.75, 29.76) * mm});
            skLineSegment(sketch, "E334", {"start": v(-356.3, 24.3) * mm, "end": v(-360.9, 15.5) * mm});
            skLineSegment(sketch, "E335", {"start": v(-366.6, 14.24) * mm, "end": v(-380.43, 24.89) * mm});
            skPoint(sketch, "E336.visualSharp", {"position": v(-382.96, 26.84) * mm});
            skArc(sketch, "E336.filletArc", {"start": v(-381.48, 29.67) * mm, "mid": v(-381.83, 27.09) * mm, "end": v(-380.43, 24.89) * mm});
            skPoint(sketch, "E337.visualSharp", {"position": v(-378.8, 34.8) * mm});
            skArc(sketch, "E337.filletArc", {"start": v(-375.89, 34.07) * mm, "mid": v(-378.37, 33.85) * mm, "end": v(-380.2, 32.14) * mm});
            skArc(sketch, "E338.filletArc", {"start": v(-356.3, 24.3) * mm, "mid": v(-356.2, 27.62) * mm, "end": v(-358.75, 29.76) * mm});
            skArc(sketch, "E339.filletArc", {"start": v(-366.6, 14.24) * mm, "mid": v(-363.46, 13.54) * mm, "end": v(-360.9, 15.5) * mm});
            skArc(sketch, "E340.MirrorCS", {"start": v(-286.86, 79.07) * mm, "mid": v(-285.33, 81.05) * mm, "end": v(-282.91, 81.66) * mm});
            skLineSegment(sketch, "E341.MirrorCS", {"start": v(-286.86, 79.07) * mm, "end": v(-292.45, 62.3) * mm});
            skArc(sketch, "E342.MirrorCS", {"start": v(-289.17, 57.3) * mm, "mid": v(-292.02, 59.01) * mm, "end": v(-292.45, 62.3) * mm});
            skLineSegment(sketch, "E343.MirrorCS", {"start": v(-289.17, 57.3) * mm, "end": v(-279.28, 56.44) * mm});
            skArc(sketch, "E344.MirrorCS", {"start": v(-275.15, 60.57) * mm, "mid": v(-276.25, 57.54) * mm, "end": v(-279.28, 56.44) * mm});
            skLineSegment(sketch, "E345.MirrorCS", {"start": v(-275.15, 60.57) * mm, "end": v(-276.67, 77.95) * mm});
            skPoint(sketch, "E346.MirrorP", {"position": v(-276.95, 81.14) * mm});
            skArc(sketch, "E347.MirrorCS", {"start": v(-255.21, 72.6) * mm, "mid": v(-253.04, 73.85) * mm, "end": v(-250.57, 73.47) * mm});
            skLineSegment(sketch, "E348.MirrorCS", {"start": v(-248.1, 72.18) * mm, "end": v(-250.57, 73.47) * mm});
            skArc(sketch, "E349.MirrorCS", {"start": v(-248.1, 72.18) * mm, "mid": v(-246.35, 70.25) * mm, "end": v(-246.24, 67.65) * mm});
            skLineSegment(sketch, "E350.MirrorCS", {"start": v(-251.54, 51.02) * mm, "end": v(-246.24, 67.65) * mm});
            skLineSegment(sketch, "E351.MirrorCS", {"start": v(-265.73, 53.42) * mm, "end": v(-256.94, 48.8) * mm});
            skArc(sketch, "E352.MirrorCS", {"start": v(-265.73, 53.42) * mm, "mid": v(-267.7, 56.09) * mm, "end": v(-266.83, 59.3) * mm});
            skLineSegment(sketch, "E353.MirrorCS", {"start": v(-255.21, 72.6) * mm, "end": v(-266.83, 59.3) * mm});
            skArc(sketch, "E354.MirrorCS", {"start": v(-280.14, 81.42) * mm, "mid": v(-277.77, 80.32) * mm, "end": v(-276.67, 77.95) * mm});
            skLineSegment(sketch, "E355.MirrorCS", {"start": v(-280.14, 81.42) * mm, "end": v(-282.91, 81.66) * mm});
            skLineSegment(sketch, "E356.MirrorCS", {"start": v(-230.08, 56.15) * mm, "end": v(-245.49, 47.5) * mm});
            skArc(sketch, "E357.MirrorCS", {"start": v(-251.54, 51.02) * mm, "mid": v(-253.73, 48.65) * mm, "end": v(-256.94, 48.8) * mm});
            skArc(sketch, "E358.MirrorCS", {"start": v(-230.08, 56.15) * mm, "mid": v(-227.62, 56.6) * mm, "end": v(-225.42, 55.42) * mm});
            skLineSegment(sketch, "E359.MirrorCS", {"start": v(-223.53, 53.37) * mm, "end": v(-225.42, 55.42) * mm});
            skArc(sketch, "E360.MirrorCS", {"start": v(-223.53, 53.37) * mm, "mid": v(-222.52, 50.97) * mm, "end": v(-223.3, 48.48) * mm});
            skLineSegment(sketch, "E361.MirrorCS", {"start": v(-233.85, 34.58) * mm, "end": v(-223.3, 48.48) * mm});
            skArc(sketch, "E362.MirrorCS", {"start": v(-233.85, 34.58) * mm, "mid": v(-236.7, 33.08) * mm, "end": v(-239.68, 34.3) * mm});
            skLineSegment(sketch, "E363.MirrorCS", {"start": v(-246.42, 41.59) * mm, "end": v(-239.68, 34.3) * mm});
            skArc(sketch, "E364.MirrorCS", {"start": v(-246.42, 41.59) * mm, "mid": v(-247.39, 44.77) * mm, "end": v(-245.49, 47.5) * mm});
            skArc(sketch, "E365.MirrorCS", {"start": v(-207.82, 29.67) * mm, "mid": v(-207.47, 27.09) * mm, "end": v(-208.87, 24.89) * mm});
            skLineSegment(sketch, "E366.MirrorCS", {"start": v(-207.82, 29.67) * mm, "end": v(-209.1, 32.14) * mm});
            skArc(sketch, "E367.MirrorCS", {"start": v(-213.41, 34.07) * mm, "mid": v(-210.93, 33.85) * mm, "end": v(-209.1, 32.14) * mm});
            skLineSegment(sketch, "E368.MirrorCS", {"start": v(-213.41, 34.07) * mm, "end": v(-230.55, 29.76) * mm});
            skArc(sketch, "E369.MirrorCS", {"start": v(-233, 24.3) * mm, "mid": v(-233.1, 27.62) * mm, "end": v(-230.55, 29.76) * mm});
            skLineSegment(sketch, "E370.MirrorCS", {"start": v(-233, 24.3) * mm, "end": v(-228.4, 15.5) * mm});
            skArc(sketch, "E371.MirrorCS", {"start": v(-222.7, 14.24) * mm, "mid": v(-225.84, 13.54) * mm, "end": v(-228.4, 15.5) * mm});
            skLineSegment(sketch, "E372.MirrorCS", {"start": v(-222.7, 14.24) * mm, "end": v(-208.87, 24.89) * mm});
            skArc(sketch, "E373.MirrorCS", {"start": v(-204.1, 7.41) * mm, "mid": v(-201.8, 6.45) * mm, "end": v(-200.58, 4.27) * mm});
            skLineSegment(sketch, "E374.MirrorCS", {"start": v(-200.1, 1.52) * mm, "end": v(-200.58, 4.27) * mm});
            skArc(sketch, "E375.MirrorCS", {"start": v(-200.1, 1.52) * mm, "mid": v(-200.55, -1.04) * mm, "end": v(-202.55, -2.72) * mm});
            skLineSegment(sketch, "E376.MirrorCS", {"start": v(-204.1, 7.41) * mm, "end": v(-221.75, 8.47) * mm});
            skArc(sketch, "E377.MirrorCS", {"start": v(-225.73, 4) * mm, "mid": v(-224.82, 7.2) * mm, "end": v(-221.75, 8.47) * mm});
            skLineSegment(sketch, "E378.MirrorCS", {"start": v(-225.73, 4) * mm, "end": v(-224, -5.77) * mm});
            skArc(sketch, "E379.MirrorCS", {"start": v(-218.95, -8.69) * mm, "mid": v(-222.16, -8.4) * mm, "end": v(-224, -5.77) * mm});
            skLineSegment(sketch, "E380.MirrorCS", {"start": v(-218.95, -8.69) * mm, "end": v(-202.55, -2.72) * mm});
            skLineSegment(sketch, "E381.MirrorCS", {"start": v(-370.35, -15.01) * mm, "end": v(-386.75, -20.98) * mm});
            skArc(sketch, "E382.MirrorCS", {"start": v(-370.35, -15.01) * mm, "mid": v(-367.14, -15.3) * mm, "end": v(-365.3, -17.93) * mm});
            skLineSegment(sketch, "E383.MirrorCS", {"start": v(-363.57, -27.7) * mm, "end": v(-365.3, -17.93) * mm});
            skArc(sketch, "E384.MirrorCS", {"start": v(-363.57, -27.7) * mm, "mid": v(-364.48, -30.9) * mm, "end": v(-367.55, -32.17) * mm});
            skLineSegment(sketch, "E385.MirrorCS", {"start": v(-385.2, -31.1) * mm, "end": v(-367.55, -32.17) * mm});
            skArc(sketch, "E386.MirrorCS", {"start": v(-385.2, -31.1) * mm, "mid": v(-387.5, -30.15) * mm, "end": v(-388.72, -27.96) * mm});
            skLineSegment(sketch, "E387.MirrorCS", {"start": v(-389.2, -25.22) * mm, "end": v(-388.72, -27.96) * mm});
            skArc(sketch, "E388.MirrorCS", {"start": v(-389.2, -25.22) * mm, "mid": v(-388.75, -22.65) * mm, "end": v(-386.75, -20.98) * mm});
            skLineSegment(sketch, "E389.MirrorCS", {"start": v(-366.6, -37.94) * mm, "end": v(-380.43, -48.58) * mm});
            skArc(sketch, "E390.MirrorCS", {"start": v(-366.6, -37.94) * mm, "mid": v(-363.46, -37.24) * mm, "end": v(-360.9, -39.2) * mm});
            skLineSegment(sketch, "E391.MirrorCS", {"start": v(-356.3, -48) * mm, "end": v(-360.9, -39.2) * mm});
            skArc(sketch, "E392.MirrorCS", {"start": v(-356.3, -48) * mm, "mid": v(-356.2, -51.32) * mm, "end": v(-358.75, -53.45) * mm});
            skLineSegment(sketch, "E393.MirrorCS", {"start": v(-375.89, -57.77) * mm, "end": v(-358.75, -53.45) * mm});
            skArc(sketch, "E394.MirrorCS", {"start": v(-375.89, -57.77) * mm, "mid": v(-378.37, -57.55) * mm, "end": v(-380.2, -55.84) * mm});
            skLineSegment(sketch, "E395.MirrorCS", {"start": v(-381.48, -53.37) * mm, "end": v(-380.2, -55.84) * mm});
            skArc(sketch, "E396.MirrorCS", {"start": v(-381.48, -53.37) * mm, "mid": v(-381.83, -50.78) * mm, "end": v(-380.43, -48.58) * mm});
            skArc(sketch, "E397.MirrorCS", {"start": v(-355.45, -58.28) * mm, "mid": v(-352.6, -56.78) * mm, "end": v(-349.62, -58) * mm});
            skLineSegment(sketch, "E398.MirrorCS", {"start": v(-355.45, -58.28) * mm, "end": v(-366, -72.18) * mm});
            skArc(sketch, "E399.MirrorCS", {"start": v(-365.77, -77.07) * mm, "mid": v(-366.78, -74.67) * mm, "end": v(-366, -72.18) * mm});
            skLineSegment(sketch, "E400.MirrorCS", {"start": v(-365.77, -77.07) * mm, "end": v(-363.88, -79.11) * mm});
            skArc(sketch, "E401.MirrorCS", {"start": v(-359.22, -79.85) * mm, "mid": v(-361.68, -80.3) * mm, "end": v(-363.88, -79.11) * mm});
            skLineSegment(sketch, "E402.MirrorCS", {"start": v(-359.22, -79.85) * mm, "end": v(-343.81, -71.2) * mm});
            skArc(sketch, "E403.MirrorCS", {"start": v(-342.88, -65.28) * mm, "mid": v(-341.91, -68.46) * mm, "end": v(-343.81, -71.2) * mm});
            skLineSegment(sketch, "E404.MirrorCS", {"start": v(-342.88, -65.28) * mm, "end": v(-349.62, -58) * mm});
            skArc(sketch, "E405.MirrorCS", {"start": v(-337.76, -74.72) * mm, "mid": v(-335.57, -72.35) * mm, "end": v(-332.36, -72.5) * mm});
            skLineSegment(sketch, "E406.MirrorCS", {"start": v(-337.76, -74.72) * mm, "end": v(-343.06, -91.35) * mm});
            skArc(sketch, "E407.MirrorCS", {"start": v(-341.2, -95.88) * mm, "mid": v(-342.95, -93.95) * mm, "end": v(-343.06, -91.35) * mm});
            skLineSegment(sketch, "E408.MirrorCS", {"start": v(-341.2, -95.88) * mm, "end": v(-338.73, -97.17) * mm});
            skArc(sketch, "E409.MirrorCS", {"start": v(-334.09, -96.3) * mm, "mid": v(-336.26, -97.54) * mm, "end": v(-338.73, -97.17) * mm});
            skLineSegment(sketch, "E410.MirrorCS", {"start": v(-334.09, -96.3) * mm, "end": v(-322.47, -83) * mm});
            skArc(sketch, "E411.MirrorCS", {"start": v(-323.57, -77.11) * mm, "mid": v(-321.6, -79.79) * mm, "end": v(-322.47, -83) * mm});
            skLineSegment(sketch, "E412.MirrorCS", {"start": v(-323.57, -77.11) * mm, "end": v(-332.36, -72.5) * mm});
            skArc(sketch, "E413.MirrorCS", {"start": v(-314.15, -84.27) * mm, "mid": v(-313.05, -81.24) * mm, "end": v(-310.02, -80.14) * mm});
            skLineSegment(sketch, "E414.MirrorCS", {"start": v(-300.13, -81) * mm, "end": v(-310.02, -80.14) * mm});
            skArc(sketch, "E415.MirrorCS", {"start": v(-300.13, -81) * mm, "mid": v(-297.28, -82.7) * mm, "end": v(-296.85, -86) * mm});
            skLineSegment(sketch, "E416.MirrorCS", {"start": v(-302.44, -102.77) * mm, "end": v(-296.85, -86) * mm});
            skPoint(sketch, "E417.MirrorP", {"position": v(-303.4, -105.62) * mm});
            skArc(sketch, "E418.MirrorCS", {"start": v(-302.44, -102.77) * mm, "mid": v(-303.97, -104.75) * mm, "end": v(-306.39, -105.36) * mm});
            skLineSegment(sketch, "E419.MirrorCS", {"start": v(-309.16, -105.11) * mm, "end": v(-306.39, -105.36) * mm});
            skArc(sketch, "E420.MirrorCS", {"start": v(-309.16, -105.11) * mm, "mid": v(-311.53, -104.01) * mm, "end": v(-312.63, -101.65) * mm});
            skLineSegment(sketch, "E421.MirrorCS", {"start": v(-314.15, -84.27) * mm, "end": v(-312.63, -101.65) * mm});
            skArc(sketch, "E422.MirrorCS", {"start": v(-289.17, -81) * mm, "mid": v(-292.02, -82.7) * mm, "end": v(-292.45, -86) * mm});
            skLineSegment(sketch, "E423.MirrorCS", {"start": v(-289.17, -81) * mm, "end": v(-279.28, -80.14) * mm});
            skArc(sketch, "E424.MirrorCS", {"start": v(-275.15, -84.27) * mm, "mid": v(-276.25, -81.24) * mm, "end": v(-279.28, -80.14) * mm});
            skLineSegment(sketch, "E425.MirrorCS", {"start": v(-275.15, -84.27) * mm, "end": v(-276.67, -101.65) * mm});
            skArc(sketch, "E426.MirrorCS", {"start": v(-280.14, -105.11) * mm, "mid": v(-277.77, -104.01) * mm, "end": v(-276.67, -101.65) * mm});
            skLineSegment(sketch, "E427.MirrorCS", {"start": v(-280.14, -105.11) * mm, "end": v(-282.91, -105.36) * mm});
            skArc(sketch, "E428.MirrorCS", {"start": v(-286.86, -102.77) * mm, "mid": v(-285.33, -104.75) * mm, "end": v(-282.91, -105.36) * mm});
            skLineSegment(sketch, "E429.MirrorCS", {"start": v(-286.86, -102.77) * mm, "end": v(-292.45, -86) * mm});
            skArc(sketch, "E430.MirrorCS", {"start": v(-265.73, -77.11) * mm, "mid": v(-267.7, -79.79) * mm, "end": v(-266.83, -83) * mm});
            skLineSegment(sketch, "E431.MirrorCS", {"start": v(-265.73, -77.11) * mm, "end": v(-256.94, -72.5) * mm});
            skArc(sketch, "E432.MirrorCS", {"start": v(-251.54, -74.72) * mm, "mid": v(-253.73, -72.35) * mm, "end": v(-256.94, -72.5) * mm});
            skArc(sketch, "E433.MirrorCS", {"start": v(-248.1, -95.88) * mm, "mid": v(-246.35, -93.95) * mm, "end": v(-246.24, -91.35) * mm});
            skLineSegment(sketch, "E434.MirrorCS", {"start": v(-248.1, -95.88) * mm, "end": v(-250.57, -97.17) * mm});
            skArc(sketch, "E435.MirrorCS", {"start": v(-255.21, -96.3) * mm, "mid": v(-253.04, -97.54) * mm, "end": v(-250.57, -97.17) * mm});
            skLineSegment(sketch, "E436.MirrorCS", {"start": v(-255.21, -96.3) * mm, "end": v(-266.83, -83) * mm});
            skLineSegment(sketch, "E437.MirrorCS", {"start": v(-246.42, -65.28) * mm, "end": v(-239.68, -58) * mm});
            skArc(sketch, "E438.MirrorCS", {"start": v(-246.42, -65.28) * mm, "mid": v(-247.39, -68.46) * mm, "end": v(-245.49, -71.2) * mm});
            skArc(sketch, "E439.MirrorCS", {"start": v(-230.08, -79.85) * mm, "mid": v(-227.62, -80.3) * mm, "end": v(-225.42, -79.11) * mm});
            skLineSegment(sketch, "E440.MirrorCS", {"start": v(-223.53, -77.07) * mm, "end": v(-225.42, -79.11) * mm});
            skArc(sketch, "E441.MirrorCS", {"start": v(-223.53, -77.07) * mm, "mid": v(-222.52, -74.67) * mm, "end": v(-223.3, -72.18) * mm});
            skLineSegment(sketch, "E442.MirrorCS", {"start": v(-233.85, -58.28) * mm, "end": v(-223.3, -72.18) * mm});
            skArc(sketch, "E443.MirrorCS", {"start": v(-233, -48) * mm, "mid": v(-233.1, -51.32) * mm, "end": v(-230.55, -53.45) * mm});
            skLineSegment(sketch, "E444.MirrorCS", {"start": v(-233, -48) * mm, "end": v(-228.4, -39.2) * mm});
            skArc(sketch, "E445.MirrorCS", {"start": v(-222.7, -37.94) * mm, "mid": v(-225.84, -37.24) * mm, "end": v(-228.4, -39.2) * mm});
            skLineSegment(sketch, "E446.MirrorCS", {"start": v(-222.7, -37.94) * mm, "end": v(-208.87, -48.58) * mm});
            skLineSegment(sketch, "E447.MirrorCS", {"start": v(-213.41, -57.77) * mm, "end": v(-230.55, -53.45) * mm});
            skArc(sketch, "E448.MirrorCS", {"start": v(-213.41, -57.77) * mm, "mid": v(-210.93, -57.55) * mm, "end": v(-209.1, -55.84) * mm});
            skLineSegment(sketch, "E449.MirrorCS", {"start": v(-207.82, -53.37) * mm, "end": v(-209.1, -55.84) * mm});
            skArc(sketch, "E450.MirrorCS", {"start": v(-207.82, -53.37) * mm, "mid": v(-207.47, -50.78) * mm, "end": v(-208.87, -48.58) * mm});
            skLineSegment(sketch, "E451.MirrorCS", {"start": v(-204.1, -31.1) * mm, "end": v(-221.75, -32.17) * mm});
            skArc(sketch, "E452.MirrorCS", {"start": v(-225.73, -27.7) * mm, "mid": v(-224.82, -30.9) * mm, "end": v(-221.75, -32.17) * mm});
            skLineSegment(sketch, "E453.MirrorCS", {"start": v(-225.73, -27.7) * mm, "end": v(-224, -17.93) * mm});
            skArc(sketch, "E454.MirrorCS", {"start": v(-218.95, -15.01) * mm, "mid": v(-222.16, -15.3) * mm, "end": v(-224, -17.93) * mm});
            skLineSegment(sketch, "E455.MirrorCS", {"start": v(-218.95, -15.01) * mm, "end": v(-202.55, -20.98) * mm});
            skArc(sketch, "E456.MirrorCS", {"start": v(-200.1, -25.22) * mm, "mid": v(-200.55, -22.65) * mm, "end": v(-202.55, -20.98) * mm});
            skLineSegment(sketch, "E457.MirrorCS", {"start": v(-200.1, -25.22) * mm, "end": v(-200.58, -27.96) * mm});
            skArc(sketch, "E458.MirrorCS", {"start": v(-204.1, -31.1) * mm, "mid": v(-201.8, -30.15) * mm, "end": v(-200.58, -27.96) * mm});
            skLineSegment(sketch, "E459.MirrorCS", {"start": v(-251.54, -74.72) * mm, "end": v(-246.24, -91.35) * mm});
            skArc(sketch, "E460.MirrorCS", {"start": v(-233.85, -58.28) * mm, "mid": v(-236.7, -56.78) * mm, "end": v(-239.68, -58) * mm});
            skLineSegment(sketch, "E461.MirrorCS", {"start": v(-230.08, -79.85) * mm, "end": v(-245.49, -71.2) * mm});
            skLineSegment(sketch, "E462", {"start": v(219.82, 146.24) * mm, "end": v(221.61, 144.1) * mm});
            skLineSegment(sketch, "E463", {"start": v(221.75, 139.4) * mm, "end": v(211.23, 125.2) * mm});
            skLineSegment(sketch, "E464", {"start": v(205.25, 125.02) * mm, "end": v(198.87, 132.62) * mm});
            skLineSegment(sketch, "E465", {"start": v(199.88, 138.37) * mm, "end": v(215, 147.1) * mm});
            skPoint(sketch, "E466.visualSharp", {"position": v(217.77, 148.7) * mm});
            skArc(sketch, "E466.filletArc", {"start": v(219.82, 146.24) * mm, "mid": v(217.56, 147.55) * mm, "end": v(215, 147.1) * mm});
            skPoint(sketch, "E467.visualSharp", {"position": v(223.54, 141.8) * mm});
            skArc(sketch, "E467.filletArc", {"start": v(221.75, 139.4) * mm, "mid": v(222.5, 141.77) * mm, "end": v(221.61, 144.1) * mm});
            skArc(sketch, "E468.filletArc", {"start": v(205.25, 125.02) * mm, "mid": v(208.28, 123.66) * mm, "end": v(211.23, 125.2) * mm});
            skArc(sketch, "E469.filletArc", {"start": v(199.88, 138.37) * mm, "mid": v(198.04, 135.73) * mm, "end": v(198.87, 132.62) * mm});
            skLineSegment(sketch, "E470", {"start": v(-42.57, 143.17) * mm, "end": v(-40.78, 145.3) * mm});
            skLineSegment(sketch, "E471", {"start": v(-36.16, 146.27) * mm, "end": v(-20.35, 138.37) * mm});
            skLineSegment(sketch, "E472", {"start": v(-19.13, 132.51) * mm, "end": v(-25.51, 124.9) * mm});
            skLineSegment(sketch, "E473", {"start": v(-31.35, 124.9) * mm, "end": v(-42.57, 138.28) * mm});
            skPoint(sketch, "E474.visualSharp", {"position": v(-44.62, 140.73) * mm});
            skArc(sketch, "E474.filletArc", {"start": v(-42.57, 143.17) * mm, "mid": v(-43.46, 140.73) * mm, "end": v(-42.57, 138.28) * mm});
            skPoint(sketch, "E475.visualSharp", {"position": v(-38.84, 147.61) * mm});
            skArc(sketch, "E475.filletArc", {"start": v(-36.16, 146.27) * mm, "mid": v(-38.63, 146.59) * mm, "end": v(-40.78, 145.3) * mm});
            skArc(sketch, "E476.filletArc", {"start": v(-19.13, 132.51) * mm, "mid": v(-18.32, 135.74) * mm, "end": v(-20.35, 138.37) * mm});
            skArc(sketch, "E477.filletArc", {"start": v(-31.35, 124.9) * mm, "mid": v(-28.43, 123.55) * mm, "end": v(-25.51, 124.9) * mm});
            skLineSegment(sketch, "E478", {"start": v(-39.71, -80.3) * mm, "end": v(-41.5, -78.16) * mm});
            skLineSegment(sketch, "E479", {"start": v(-41.65, -73.44) * mm, "end": v(-31.12, -59.25) * mm});
            skLineSegment(sketch, "E480", {"start": v(-25.14, -59.07) * mm, "end": v(-18.76, -66.67) * mm});
            skLineSegment(sketch, "E481", {"start": v(-19.78, -72.42) * mm, "end": v(-34.89, -81.15) * mm});
            skPoint(sketch, "E482.visualSharp", {"position": v(-37.66, -82.75) * mm});
            skArc(sketch, "E482.filletArc", {"start": v(-39.71, -80.3) * mm, "mid": v(-37.46, -81.6) * mm, "end": v(-34.89, -81.15) * mm});
            skPoint(sketch, "E483.visualSharp", {"position": v(-43.44, -75.86) * mm});
            skArc(sketch, "E483.filletArc", {"start": v(-41.65, -73.44) * mm, "mid": v(-42.4, -75.83) * mm, "end": v(-41.5, -78.16) * mm});
            skArc(sketch, "E484.filletArc", {"start": v(-25.14, -59.07) * mm, "mid": v(-28.18, -57.7) * mm, "end": v(-31.12, -59.25) * mm});
            skArc(sketch, "E485.filletArc", {"start": v(-19.78, -72.42) * mm, "mid": v(-17.93, -69.78) * mm, "end": v(-18.76, -66.67) * mm});
            skLineSegment(sketch, "E486", {"start": v(222.4, -78.09) * mm, "end": v(220.6, -80.22) * mm});
            skLineSegment(sketch, "E487", {"start": v(215.98, -81.18) * mm, "end": v(200.17, -73.28) * mm});
            skLineSegment(sketch, "E488", {"start": v(198.96, -67.43) * mm, "end": v(205.34, -59.82) * mm});
            skLineSegment(sketch, "E489", {"start": v(211.17, -59.82) * mm, "end": v(222.4, -73.19) * mm});
            skPoint(sketch, "E490.visualSharp", {"position": v(224.45, -75.64) * mm});
            skArc(sketch, "E490.filletArc", {"start": v(222.4, -78.09) * mm, "mid": v(223.28, -75.64) * mm, "end": v(222.4, -73.19) * mm});
            skPoint(sketch, "E491.visualSharp", {"position": v(218.67, -82.53) * mm});
            skArc(sketch, "E491.filletArc", {"start": v(215.98, -81.18) * mm, "mid": v(218.46, -81.5) * mm, "end": v(220.6, -80.22) * mm});
            skArc(sketch, "E492.filletArc", {"start": v(198.96, -67.43) * mm, "mid": v(198.14, -70.65) * mm, "end": v(200.17, -73.28) * mm});
            skArc(sketch, "E493.filletArc", {"start": v(211.17, -59.82) * mm, "mid": v(208.26, -58.46) * mm, "end": v(205.34, -59.82) * mm});
            skLineSegment(sketch, "E494", {"start": v(-188.91, 214.09) * mm, "end": v(-186.13, 214.09) * mm});
            skLineSegment(sketch, "E495", {"start": v(-182.42, 211.16) * mm, "end": v(-178.31, 193.98) * mm});
            skLineSegment(sketch, "E496", {"start": v(-182.02, 189.28) * mm, "end": v(-191.94, 189.28) * mm});
            skLineSegment(sketch, "E497", {"start": v(-195.7, 193.75) * mm, "end": v(-192.66, 210.94) * mm});
            skPoint(sketch, "E498.visualSharp", {"position": v(-192.1, 214.09) * mm});
            skArc(sketch, "E498.filletArc", {"start": v(-188.91, 214.09) * mm, "mid": v(-191.36, 213.2) * mm, "end": v(-192.66, 210.94) * mm});
            skPoint(sketch, "E499.visualSharp", {"position": v(-183.12, 214.09) * mm});
            skArc(sketch, "E499.filletArc", {"start": v(-182.42, 211.16) * mm, "mid": v(-183.77, 213.27) * mm, "end": v(-186.13, 214.09) * mm});
            skArc(sketch, "E500.filletArc", {"start": v(-182.02, 189.28) * mm, "mid": v(-179.03, 190.73) * mm, "end": v(-178.31, 193.98) * mm});
            skArc(sketch, "E501.filletArc", {"start": v(-195.7, 193.75) * mm, "mid": v(-194.86, 190.64) * mm, "end": v(-191.94, 189.28) * mm});
            skSolve(sketch);
        }
        {
            var Q0;
            Q0=makeQuery(id+"F0.imprint","IMPRINT",FACE,{"disambiguationData":[TD([[makeQuery(id+"F0.imprint","IMPRINT",EDGE,{"derivedFrom":sQuery(id+"F0.wireOp",EDGE,"E1")}),-1.0]])]});
            var Q1;
            Q1=makeQuery(id+"F0.imprint","IMPRINT",FACE,{"disambiguationData":[TD([[makeQuery(id+"F0.imprint","IMPRINT",EDGE,{"derivedFrom":sQuery(id+"F0.wireOp",EDGE,"E462")}),-1.0]])]});
            var Q2;
            {var subQ0=sQuery(id+"F0.wireOp",EDGE,"E111.MirrorCS");Q2=makeQuery(id+"F0.imprint","IMPRINT",FACE,{"disambiguationData":[TD([[makeQuery(id+"F0.imprint","IMPRINT",EDGE,{"derivedFrom":subQ0}),-1.0]])]});}
            var Q3;
            Q3=makeQuery(id+"F0.imprint","IMPRINT",FACE,{"disambiguationData":[TD([[makeQuery(id+"F0.imprint","IMPRINT",EDGE,{"derivedFrom":sQuery(id+"F0.wireOp",EDGE,"E464")}),-1.0]])]});
            var Q4;
            {var subQ5=sQuery(id+"F0.wireOp",EDGE,"E117.MirrorCS");Q4=makeQuery(id+"F0.imprint","IMPRINT",FACE,{"disambiguationData":[TD([[makeQuery(id+"F0.imprint","IMPRINT",EDGE,{"derivedFrom":subQ5}),-1.0]])]});}
            var Q5;
            {var subQ5=sQuery(id+"F0.wireOp",EDGE,"E108.MirrorCS");Q5=makeQuery(id+"F0.imprint","IMPRINT",FACE,{"disambiguationData":[TD([[makeQuery(id+"F0.imprint","IMPRINT",EDGE,{"derivedFrom":subQ5}),-1.0]])]});}
            var Q6;
            {var subQ5=sQuery(id+"F0.wireOp",EDGE,"E102.MirrorCS");Q6=makeQuery(id+"F0.imprint","IMPRINT",FACE,{"disambiguationData":[TD([[makeQuery(id+"F0.imprint","IMPRINT",EDGE,{"derivedFrom":subQ5}),-1.0]])]});}
            var Q7;
            {var subQ5=sQuery(id+"F0.wireOp",EDGE,"E100.MirrorCS");Q7=makeQuery(id+"F0.imprint","IMPRINT",FACE,{"disambiguationData":[TD([[makeQuery(id+"F0.imprint","IMPRINT",EDGE,{"derivedFrom":subQ5}),-1.0]])]});}
            var Q8;
            Q8=makeQuery(id+"F0.imprint","IMPRINT",FACE,{"disambiguationData":[TD([[makeQuery(id+"F0.imprint","IMPRINT",EDGE,{"derivedFrom":sQuery(id+"F0.wireOp",EDGE,"E95.MirrorCS")}),1.0]])]});
            var Q9;
            {var subQ5=sQuery(id+"F0.wireOp",EDGE,"E91.MirrorCS");Q9=makeQuery(id+"F0.imprint","IMPRINT",FACE,{"disambiguationData":[TD([[makeQuery(id+"F0.imprint","IMPRINT",EDGE,{"derivedFrom":subQ5}),-1.0]])]});}
            var Q10;
            {var subQ4=sQuery(id+"F0.wireOp",EDGE,"E78.MirrorCS");Q10=makeQuery(id+"F0.imprint","IMPRINT",FACE,{"disambiguationData":[TD([[makeQuery(id+"F0.imprint","IMPRINT",EDGE,{"derivedFrom":subQ4}),-1.0]])]});}
            var Q11;
            Q11=makeQuery(id+"F0.imprint","IMPRINT",FACE,{"disambiguationData":[TD([[makeQuery(id+"F0.imprint","IMPRINT",EDGE,{"derivedFrom":sQuery(id+"F0.wireOp",EDGE,"E86.MirrorCS")}),1.0]])]});
            var Q12;
            {var subQ5=sQuery(id+"F0.wireOp",EDGE,"E81.MirrorCS");Q12=makeQuery(id+"F0.imprint","IMPRINT",FACE,{"disambiguationData":[TD([[makeQuery(id+"F0.imprint","IMPRINT",EDGE,{"derivedFrom":subQ5}),-1.0]])]});}
            var Q13;
            {var subQ5=sQuery(id+"F0.wireOp",EDGE,"E71.MirrorCS");Q13=makeQuery(id+"F0.imprint","IMPRINT",FACE,{"disambiguationData":[TD([[makeQuery(id+"F0.imprint","IMPRINT",EDGE,{"derivedFrom":subQ5}),1.0]])]});}
            var Q14;
            {var subQ0=sQuery(id+"F0.wireOp",EDGE,"E73.MirrorCS");Q14=makeQuery(id+"F0.imprint","IMPRINT",FACE,{"disambiguationData":[TD([[makeQuery(id+"F0.imprint","IMPRINT",EDGE,{"derivedFrom":subQ0}),1.0]])]});}
            var Q15;
            {var subQ0=sQuery(id+"F0.wireOp",EDGE,"E62.MirrorCS");Q15=makeQuery(id+"F0.imprint","IMPRINT",FACE,{"disambiguationData":[TD([[makeQuery(id+"F0.imprint","IMPRINT",EDGE,{"derivedFrom":subQ0}),1.0]])]});}
            var Q16;
            {var subQ5=sQuery(id+"F0.wireOp",EDGE,"E68.MirrorCS");Q16=makeQuery(id+"F0.imprint","IMPRINT",FACE,{"disambiguationData":[TD([[makeQuery(id+"F0.imprint","IMPRINT",EDGE,{"derivedFrom":subQ5}),1.0]])]});}
            var Q17;
            {var subQ1=sQuery(id+"F0.wireOp",EDGE,"E57.MirrorCS");Q17=makeQuery(id+"F0.imprint","IMPRINT",FACE,{"disambiguationData":[TD([[makeQuery(id+"F0.imprint","IMPRINT",EDGE,{"derivedFrom":subQ1}),1.0]])]});}
            var Q18;
            {var subQ5=sQuery(id+"F0.wireOp",EDGE,"E55.MirrorCS");Q18=makeQuery(id+"F0.imprint","IMPRINT",FACE,{"disambiguationData":[TD([[makeQuery(id+"F0.imprint","IMPRINT",EDGE,{"derivedFrom":subQ5}),1.0]])]});}
            var Q19;
            {var subQ0=sQuery(id+"F0.wireOp",EDGE,"E48.MirrorCS");Q19=makeQuery(id+"F0.imprint","IMPRINT",FACE,{"disambiguationData":[TD([[makeQuery(id+"F0.imprint","IMPRINT",EDGE,{"derivedFrom":subQ0}),1.0]])]});}
            var Q20;
            {var subQ5=sQuery(id+"F0.wireOp",EDGE,"E45.MirrorCS");Q20=makeQuery(id+"F0.imprint","IMPRINT",FACE,{"disambiguationData":[TD([[makeQuery(id+"F0.imprint","IMPRINT",EDGE,{"derivedFrom":subQ5}),1.0]])]});}
            var Q21;
            {var subQ0=sQuery(id+"F0.wireOp",EDGE,"E37.MirrorCS");Q21=makeQuery(id+"F0.imprint","IMPRINT",FACE,{"disambiguationData":[TD([[makeQuery(id+"F0.imprint","IMPRINT",EDGE,{"derivedFrom":subQ0}),1.0]])]});}
            var Q22;
            {var subQ5=sQuery(id+"F0.wireOp",EDGE,"E472");Q22=makeQuery(id+"F0.imprint","IMPRINT",FACE,{"disambiguationData":[TD([[makeQuery(id+"F0.imprint","IMPRINT",EDGE,{"derivedFrom":subQ5}),-1.0]])]});}
            var Q23;
            {var subQ5=sQuery(id+"F0.wireOp",EDGE,"E36.MirrorCS");Q23=makeQuery(id+"F0.imprint","IMPRINT",FACE,{"disambiguationData":[TD([[makeQuery(id+"F0.imprint","IMPRINT",EDGE,{"derivedFrom":subQ5}),1.0]])]});}
            var Q24;
            Q24=makeQuery(id+"F0.imprint","IMPRINT",FACE,{"disambiguationData":[TD([[makeQuery(id+"F0.imprint","IMPRINT",EDGE,{"derivedFrom":sQuery(id+"F0.wireOp",EDGE,"E470")}),-1.0]])]});
            var Q25;
            Q25=makeQuery(id+"F0.imprint","IMPRINT",FACE,{"disambiguationData":[TD([[makeQuery(id+"F0.imprint","IMPRINT",EDGE,{"derivedFrom":sQuery(id+"F0.wireOp",EDGE,"E20")}),-1.0]])]});
            var Q26;
            {var subQ5=sQuery(id+"F0.wireOp",EDGE,"E22");Q26=makeQuery(id+"F0.imprint","IMPRINT",FACE,{"disambiguationData":[TD([[makeQuery(id+"F0.imprint","IMPRINT",EDGE,{"derivedFrom":subQ5}),-1.0]])]});}
            var Q27;
            Q27=makeQuery(id+"F0.imprint","IMPRINT",FACE,{"disambiguationData":[TD([[makeQuery(id+"F0.imprint","IMPRINT",EDGE,{"derivedFrom":sQuery(id+"F0.wireOp",EDGE,"E12")}),-1.0]])]});
            var Q28;
            {var subQ5=sQuery(id+"F0.wireOp",EDGE,"E14");Q28=makeQuery(id+"F0.imprint","IMPRINT",FACE,{"disambiguationData":[TD([[makeQuery(id+"F0.imprint","IMPRINT",EDGE,{"derivedFrom":subQ5}),-1.0]])]});}
            var Q29;
            {var subQ5=sQuery(id+"F0.wireOp",EDGE,"E30");Q29=makeQuery(id+"F0.imprint","IMPRINT",FACE,{"disambiguationData":[TD([[makeQuery(id+"F0.imprint","IMPRINT",EDGE,{"derivedFrom":subQ5}),-1.0]])]});}
            var Q30;
            Q30=makeQuery(id+"F0.imprint","IMPRINT",FACE,{"disambiguationData":[TD([[makeQuery(id+"F0.imprint","IMPRINT",EDGE,{"derivedFrom":sQuery(id+"F0.wireOp",EDGE,"E28")}),-1.0]])]});
            var Q31;
            Q31=makeQuery(id+"F0.imprint","IMPRINT",FACE,{"disambiguationData":[TD([[makeQuery(id+"F0.imprint","IMPRINT",EDGE,{"derivedFrom":sQuery(id+"F0.wireOp",EDGE,"E4")}),-1.0]])]});
            var Q32;
            {var subQ5=sQuery(id+"F0.wireOp",EDGE,"E6");Q32=makeQuery(id+"F0.imprint","IMPRINT",FACE,{"disambiguationData":[TD([[makeQuery(id+"F0.imprint","IMPRINT",EDGE,{"derivedFrom":subQ5}),-1.0]])]});}
            var Q33;
            {var subQ5=sQuery(id+"F0.wireOp",EDGE,"E151.MirrorCS");Q33=makeQuery(id+"F0.imprint","IMPRINT",FACE,{"disambiguationData":[TD([[makeQuery(id+"F0.imprint","IMPRINT",EDGE,{"derivedFrom":subQ5}),1.0]])]});}
            var Q34;
            {var subQ0=sQuery(id+"F0.wireOp",EDGE,"E153.MirrorCS");Q34=makeQuery(id+"F0.imprint","IMPRINT",FACE,{"disambiguationData":[TD([[makeQuery(id+"F0.imprint","IMPRINT",EDGE,{"derivedFrom":subQ0}),1.0]])]});}
            var Q35;
            {var subQ0=sQuery(id+"F0.wireOp",EDGE,"E160.MirrorCS");Q35=makeQuery(id+"F0.imprint","IMPRINT",FACE,{"disambiguationData":[TD([[makeQuery(id+"F0.imprint","IMPRINT",EDGE,{"derivedFrom":subQ0}),1.0]])]});}
            var Q36;
            {var subQ5=sQuery(id+"F0.wireOp",EDGE,"E167.MirrorCS");Q36=makeQuery(id+"F0.imprint","IMPRINT",FACE,{"disambiguationData":[TD([[makeQuery(id+"F0.imprint","IMPRINT",EDGE,{"derivedFrom":subQ5}),1.0]])]});}
            var Q37;
            {var subQ0=sQuery(id+"F0.wireOp",EDGE,"E172.MirrorCS");Q37=makeQuery(id+"F0.imprint","IMPRINT",FACE,{"disambiguationData":[TD([[makeQuery(id+"F0.imprint","IMPRINT",EDGE,{"derivedFrom":subQ0}),1.0]])]});}
            var Q38;
            {var subQ5=sQuery(id+"F0.wireOp",EDGE,"E170.MirrorCS");Q38=makeQuery(id+"F0.imprint","IMPRINT",FACE,{"disambiguationData":[TD([[makeQuery(id+"F0.imprint","IMPRINT",EDGE,{"derivedFrom":subQ5}),1.0]])]});}
            var Q39;
            {var subQ0=sQuery(id+"F0.wireOp",EDGE,"E180.MirrorCS");Q39=makeQuery(id+"F0.imprint","IMPRINT",FACE,{"disambiguationData":[TD([[makeQuery(id+"F0.imprint","IMPRINT",EDGE,{"derivedFrom":subQ0}),1.0]])]});}
            var Q40;
            {var subQ5=sQuery(id+"F0.wireOp",EDGE,"E190.MirrorCS");Q40=makeQuery(id+"F0.imprint","IMPRINT",FACE,{"disambiguationData":[TD([[makeQuery(id+"F0.imprint","IMPRINT",EDGE,{"derivedFrom":subQ5}),1.0]])]});}
            var Q41;
            Q41=makeQuery(id+"F0.imprint","IMPRINT",FACE,{"disambiguationData":[TD([[makeQuery(id+"F0.imprint","IMPRINT",EDGE,{"derivedFrom":sQuery(id+"F0.wireOp",EDGE,"E478")}),-1.0]])]});
            var Q42;
            {var subQ5=sQuery(id+"F0.wireOp",EDGE,"E480");Q42=makeQuery(id+"F0.imprint","IMPRINT",FACE,{"disambiguationData":[TD([[makeQuery(id+"F0.imprint","IMPRINT",EDGE,{"derivedFrom":subQ5}),-1.0]])]});}
            var Q43;
            {var subQ5=sQuery(id+"F0.wireOp",EDGE,"E186.MirrorCS");Q43=makeQuery(id+"F0.imprint","IMPRINT",FACE,{"disambiguationData":[TD([[makeQuery(id+"F0.imprint","IMPRINT",EDGE,{"derivedFrom":subQ5}),-1.0]])]});}
            var Q44;
            {var subQ0=sQuery(id+"F0.wireOp",EDGE,"E188.MirrorCS");Q44=makeQuery(id+"F0.imprint","IMPRINT",FACE,{"disambiguationData":[TD([[makeQuery(id+"F0.imprint","IMPRINT",EDGE,{"derivedFrom":subQ0}),-1.0]])]});}
            var Q45;
            {var subQ5=sQuery(id+"F0.wireOp",EDGE,"E202.MirrorCS");Q45=makeQuery(id+"F0.imprint","IMPRINT",FACE,{"disambiguationData":[TD([[makeQuery(id+"F0.imprint","IMPRINT",EDGE,{"derivedFrom":subQ5}),-1.0]])]});}
            var Q46;
            {var subQ0=sQuery(id+"F0.wireOp",EDGE,"E196.MirrorCS");Q46=makeQuery(id+"F0.imprint","IMPRINT",FACE,{"disambiguationData":[TD([[makeQuery(id+"F0.imprint","IMPRINT",EDGE,{"derivedFrom":subQ0}),-1.0]])]});}
            var Q47;
            {var subQ5=sQuery(id+"F0.wireOp",EDGE,"E204.MirrorCS");Q47=makeQuery(id+"F0.imprint","IMPRINT",FACE,{"disambiguationData":[TD([[makeQuery(id+"F0.imprint","IMPRINT",EDGE,{"derivedFrom":subQ5}),-1.0]])]});}
            var Q48;
            {var subQ5=sQuery(id+"F0.wireOp",EDGE,"E213.MirrorCS");Q48=makeQuery(id+"F0.imprint","IMPRINT",FACE,{"disambiguationData":[TD([[makeQuery(id+"F0.imprint","IMPRINT",EDGE,{"derivedFrom":subQ5}),-1.0]])]});}
            var Q49;
            {var subQ5=sQuery(id+"F0.wireOp",EDGE,"E229.MirrorCS");Q49=makeQuery(id+"F0.imprint","IMPRINT",FACE,{"disambiguationData":[TD([[makeQuery(id+"F0.imprint","IMPRINT",EDGE,{"derivedFrom":subQ5}),1.0]])]});}
            var Q50;
            {var subQ5=sQuery(id+"F0.wireOp",EDGE,"E221.MirrorCS");Q50=makeQuery(id+"F0.imprint","IMPRINT",FACE,{"disambiguationData":[TD([[makeQuery(id+"F0.imprint","IMPRINT",EDGE,{"derivedFrom":subQ5}),-1.0]])]});}
            var Q51;
            {var subQ0=sQuery(id+"F0.wireOp",EDGE,"E215.MirrorCS");Q51=makeQuery(id+"F0.imprint","IMPRINT",FACE,{"disambiguationData":[TD([[makeQuery(id+"F0.imprint","IMPRINT",EDGE,{"derivedFrom":subQ0}),-1.0]])]});}
            var Q52;
            {var subQ4=sQuery(id+"F0.wireOp",EDGE,"E227.MirrorCS");Q52=makeQuery(id+"F0.imprint","IMPRINT",FACE,{"disambiguationData":[TD([[makeQuery(id+"F0.imprint","IMPRINT",EDGE,{"derivedFrom":subQ4}),1.0]])]});}
            var Q53;
            {var subQ0=sQuery(id+"F0.wireOp",EDGE,"E223.MirrorCS");Q53=makeQuery(id+"F0.imprint","IMPRINT",FACE,{"disambiguationData":[TD([[makeQuery(id+"F0.imprint","IMPRINT",EDGE,{"derivedFrom":subQ0}),-1.0]])]});}
            var Q54;
            {var subQ0=sQuery(id+"F0.wireOp",EDGE,"E206.MirrorCS");Q54=makeQuery(id+"F0.imprint","IMPRINT",FACE,{"disambiguationData":[TD([[makeQuery(id+"F0.imprint","IMPRINT",EDGE,{"derivedFrom":subQ0}),-1.0]])]});}
            var Q55;
            {var subQ5=sQuery(id+"F0.wireOp",EDGE,"E240.MirrorCS");Q55=makeQuery(id+"F0.imprint","IMPRINT",FACE,{"disambiguationData":[TD([[makeQuery(id+"F0.imprint","IMPRINT",EDGE,{"derivedFrom":subQ5}),1.0]])]});}
            var Q56;
            {var subQ5=sQuery(id+"F0.wireOp",EDGE,"E290.MirrorCS");Q56=makeQuery(id+"F0.imprint","IMPRINT",FACE,{"disambiguationData":[TD([[makeQuery(id+"F0.imprint","IMPRINT",EDGE,{"derivedFrom":subQ5}),1.0]])]});}
            var Q57;
            {var subQ5=sQuery(id+"F0.wireOp",EDGE,"E291.MirrorCS");Q57=makeQuery(id+"F0.imprint","IMPRINT",FACE,{"disambiguationData":[TD([[makeQuery(id+"F0.imprint","IMPRINT",EDGE,{"derivedFrom":subQ5}),1.0]])]});}
            var Q58;
            {var subQ5=sQuery(id+"F0.wireOp",EDGE,"E488");Q58=makeQuery(id+"F0.imprint","IMPRINT",FACE,{"disambiguationData":[TD([[makeQuery(id+"F0.imprint","IMPRINT",EDGE,{"derivedFrom":subQ5}),-1.0]])]});}
            var Q59;
            {var subQ5=sQuery(id+"F0.wireOp",EDGE,"E258.MirrorCS");Q59=makeQuery(id+"F0.imprint","IMPRINT",FACE,{"disambiguationData":[TD([[makeQuery(id+"F0.imprint","IMPRINT",EDGE,{"derivedFrom":subQ5}),1.0]])]});}
            var Q60;
            Q60=makeQuery(id+"F0.imprint","IMPRINT",FACE,{"disambiguationData":[TD([[makeQuery(id+"F0.imprint","IMPRINT",EDGE,{"derivedFrom":sQuery(id+"F0.wireOp",EDGE,"E236.MirrorCS")}),1.0]])]});
            var Q61;
            Q61=makeQuery(id+"F0.imprint","IMPRINT",FACE,{"disambiguationData":[TD([[makeQuery(id+"F0.imprint","IMPRINT",EDGE,{"derivedFrom":sQuery(id+"F0.wireOp",EDGE,"E244.MirrorCS")}),-1.0]])]});
            var Q62;
            Q62=makeQuery(id+"F0.imprint","IMPRINT",FACE,{"disambiguationData":[TD([[makeQuery(id+"F0.imprint","IMPRINT",EDGE,{"derivedFrom":sQuery(id+"F0.wireOp",EDGE,"E250.MirrorCS")}),-1.0]])]});
            var Q63;
            Q63=makeQuery(id+"F0.imprint","IMPRINT",FACE,{"disambiguationData":[TD([[makeQuery(id+"F0.imprint","IMPRINT",EDGE,{"derivedFrom":sQuery(id+"F0.wireOp",EDGE,"E486")}),-1.0]])]});
            var Q64;
            {var subQ0=sQuery(id+"F0.wireOp",EDGE,"E260.MirrorCS");Q64=makeQuery(id+"F0.imprint","IMPRINT",FACE,{"disambiguationData":[TD([[makeQuery(id+"F0.imprint","IMPRINT",EDGE,{"derivedFrom":subQ0}),1.0]])]});}
            var Q65;
            Q65=makeQuery(id+"F0.imprint","IMPRINT",FACE,{"disambiguationData":[TD([[makeQuery(id+"F0.imprint","IMPRINT",EDGE,{"derivedFrom":sQuery(id+"F0.wireOp",EDGE,"E263.MirrorCS")}),1.0]])]});
            var Q66;
            {var subQ0=sQuery(id+"F0.wireOp",EDGE,"E280.MirrorCS");Q66=makeQuery(id+"F0.imprint","IMPRINT",FACE,{"disambiguationData":[TD([[makeQuery(id+"F0.imprint","IMPRINT",EDGE,{"derivedFrom":subQ0}),-1.0]])]});}
            var Q67;
            {var subQ2=sQuery(id+"F0.wireOp",EDGE,"E283.MirrorCS");Q67=makeQuery(id+"F0.imprint","IMPRINT",FACE,{"disambiguationData":[TD([[makeQuery(id+"F0.imprint","IMPRINT",EDGE,{"derivedFrom":subQ2}),-1.0]])]});}
            var Q68;
            {var subQ5=sQuery(id+"F0.wireOp",EDGE,"E269.MirrorCS");Q68=makeQuery(id+"F0.imprint","IMPRINT",FACE,{"disambiguationData":[TD([[makeQuery(id+"F0.imprint","IMPRINT",EDGE,{"derivedFrom":subQ5}),-1.0]])]});}
            var Q69;
            {var subQ5=sQuery(id+"F0.wireOp",EDGE,"E271.MirrorCS");Q69=makeQuery(id+"F0.imprint","IMPRINT",FACE,{"disambiguationData":[TD([[makeQuery(id+"F0.imprint","IMPRINT",EDGE,{"derivedFrom":subQ5}),-1.0]])]});}
            var Q70;
            {var subQ5=sQuery(id+"F0.wireOp",EDGE,"E267.MirrorCS");Q70=makeQuery(id+"F0.imprint","IMPRINT",FACE,{"disambiguationData":[TD([[makeQuery(id+"F0.imprint","IMPRINT",EDGE,{"derivedFrom":subQ5}),-1.0]])]});}
            var Q71;
            {var subQ5=sQuery(id+"F0.wireOp",EDGE,"E298.MirrorCS");Q71=makeQuery(id+"F0.imprint","IMPRINT",FACE,{"disambiguationData":[TD([[makeQuery(id+"F0.imprint","IMPRINT",EDGE,{"derivedFrom":subQ5}),-1.0]])]});}
            var Q72;
            {var subQ5=sQuery(id+"F0.wireOp",EDGE,"E284.MirrorCS");Q72=makeQuery(id+"F0.imprint","IMPRINT",FACE,{"disambiguationData":[TD([[makeQuery(id+"F0.imprint","IMPRINT",EDGE,{"derivedFrom":subQ5}),-1.0]])]});}
            var Q73;
            {var subQ5=sQuery(id+"F0.wireOp",EDGE,"E149.MirrorCS");Q73=makeQuery(id+"F0.imprint","IMPRINT",FACE,{"disambiguationData":[TD([[makeQuery(id+"F0.imprint","IMPRINT",EDGE,{"derivedFrom":subQ5}),1.0]])]});}
            var Q74;
            {var subQ0=sQuery(id+"F0.wireOp",EDGE,"E147.MirrorCS");Q74=makeQuery(id+"F0.imprint","IMPRINT",FACE,{"disambiguationData":[TD([[makeQuery(id+"F0.imprint","IMPRINT",EDGE,{"derivedFrom":subQ0}),1.0]])]});}
            var Q75;
            {var subQ0=sQuery(id+"F0.wireOp",EDGE,"E135.MirrorCS");Q75=makeQuery(id+"F0.imprint","IMPRINT",FACE,{"disambiguationData":[TD([[makeQuery(id+"F0.imprint","IMPRINT",EDGE,{"derivedFrom":subQ0}),1.0]])]});}
            var Q76;
            {var subQ0=sQuery(id+"F0.wireOp",EDGE,"E125.MirrorCS");Q76=makeQuery(id+"F0.imprint","IMPRINT",FACE,{"disambiguationData":[TD([[makeQuery(id+"F0.imprint","IMPRINT",EDGE,{"derivedFrom":subQ0}),1.0]])]});}
            var Q77;
            {var subQ5=sQuery(id+"F0.wireOp",EDGE,"E132.MirrorCS");Q77=makeQuery(id+"F0.imprint","IMPRINT",FACE,{"disambiguationData":[TD([[makeQuery(id+"F0.imprint","IMPRINT",EDGE,{"derivedFrom":subQ5}),1.0]])]});}
            var Q78;
            {var subQ5=sQuery(id+"F0.wireOp",EDGE,"E141.MirrorCS");Q78=makeQuery(id+"F0.imprint","IMPRINT",FACE,{"disambiguationData":[TD([[makeQuery(id+"F0.imprint","IMPRINT",EDGE,{"derivedFrom":subQ5}),1.0]])]});}
            var Q79;
            {var subQ0=sQuery(id+"F0.wireOp",EDGE,"E118.MirrorCS");Q79=makeQuery(id+"F0.imprint","IMPRINT",FACE,{"disambiguationData":[TD([[makeQuery(id+"F0.imprint","IMPRINT",EDGE,{"derivedFrom":subQ0}),1.0]])]});}
            extrude(context, id + "F1", {"entities" : qUnion([Q0, Q1, Q2, Q3, Q4, Q5, Q6, Q7, Q8, Q9, Q10, Q11, Q12, Q13, Q14, Q15, Q16, Q17, Q18, Q19, Q20, Q21, Q22, Q23, Q24, Q25, Q26, Q27, Q28, Q29, Q30, Q31, Q32, Q33, Q34, Q35, Q36, Q37, Q38, Q39, Q40, Q41, Q42, Q43, Q44, Q45, Q46, Q47, Q48, Q49, Q50, Q51, Q52, Q53, Q54, Q55, Q56, Q57, Q58, Q59, Q60, Q61, Q62, Q63, Q64, Q65, Q66, Q67, Q68, Q69, Q70, Q71, Q72, Q73, Q74, Q75, Q76, Q77, Q78, Q79]), "depth" : 12.7 * mm});
        }
        {
            var Q0;
            Q0=qCreatedBy(makeId("Front.planeOp"),FACE);
            var sketch = newSketch(context, id + "F2", { "sketchPlane" : qUnion([Q0])});
            skCircle(sketch, "E502", {"center": v(-247.7, 49.62) * mm, "radius": 76.2 * mm});
            skCircle(sketch, "E503", {"center": v(-247.7, 49.62) * mm, "radius": 6.35 * mm});
            skLineSegment(sketch, "E504", {"start": v(-342.24, 63) * mm, "end": v(-341.76, 65.73) * mm});
            skLineSegment(sketch, "E505", {"start": v(-338.24, 68.88) * mm, "end": v(-320.6, 69.94) * mm});
            skLineSegment(sketch, "E506", {"start": v(-316.62, 65.47) * mm, "end": v(-318.34, 55.7) * mm});
            skLineSegment(sketch, "E507", {"start": v(-323.4, 52.78) * mm, "end": v(-339.8, 58.75) * mm});
            skPoint(sketch, "E508.visualSharp", {"position": v(-342.8, 59.84) * mm});
            skArc(sketch, "E508.filletArc", {"start": v(-342.24, 63) * mm, "mid": v(-341.79, 60.42) * mm, "end": v(-339.8, 58.75) * mm});
            skPoint(sketch, "E509.visualSharp", {"position": v(-341.24, 68.7) * mm});
            skArc(sketch, "E509.filletArc", {"start": v(-338.24, 68.88) * mm, "mid": v(-340.54, 67.92) * mm, "end": v(-341.76, 65.73) * mm});
            skArc(sketch, "E510.filletArc", {"start": v(-316.62, 65.47) * mm, "mid": v(-317.52, 68.67) * mm, "end": v(-320.6, 69.94) * mm});
            skArc(sketch, "E511.filletArc", {"start": v(-323.4, 52.78) * mm, "mid": v(-320.19, 53.06) * mm, "end": v(-318.34, 55.7) * mm});
            skLineSegment(sketch, "E512", {"start": v(-262.2, 142.88) * mm, "end": v(-259.43, 143.13) * mm});
            skLineSegment(sketch, "E513", {"start": v(-255.48, 140.54) * mm, "end": v(-249.9, 123.77) * mm});
            skLineSegment(sketch, "E514", {"start": v(-253.17, 118.77) * mm, "end": v(-263.06, 117.9) * mm});
            skLineSegment(sketch, "E515", {"start": v(-267.2, 122.04) * mm, "end": v(-265.67, 139.42) * mm});
            skPoint(sketch, "E516.visualSharp", {"position": v(-265.4, 142.6) * mm});
            skArc(sketch, "E516.filletArc", {"start": v(-262.2, 142.88) * mm, "mid": v(-264.57, 141.78) * mm, "end": v(-265.67, 139.42) * mm});
            skPoint(sketch, "E517.visualSharp", {"position": v(-256.44, 143.39) * mm});
            skArc(sketch, "E517.filletArc", {"start": v(-255.48, 140.54) * mm, "mid": v(-257, 142.52) * mm, "end": v(-259.43, 143.13) * mm});
            skArc(sketch, "E518.filletArc", {"start": v(-253.17, 118.77) * mm, "mid": v(-250.32, 120.48) * mm, "end": v(-249.9, 123.77) * mm});
            skArc(sketch, "E519.filletArc", {"start": v(-267.2, 122.04) * mm, "mid": v(-266.09, 119) * mm, "end": v(-263.06, 117.9) * mm});
            skLineSegment(sketch, "E520", {"start": v(-318.81, 114.84) * mm, "end": v(-316.92, 116.88) * mm});
            skLineSegment(sketch, "E521", {"start": v(-312.26, 117.62) * mm, "end": v(-296.85, 108.96) * mm});
            skLineSegment(sketch, "E522", {"start": v(-295.92, 103.05) * mm, "end": v(-302.66, 95.77) * mm});
            skLineSegment(sketch, "E523", {"start": v(-308.5, 96.05) * mm, "end": v(-319.05, 109.95) * mm});
            skPoint(sketch, "E524.visualSharp", {"position": v(-320.99, 112.5) * mm});
            skArc(sketch, "E524.filletArc", {"start": v(-318.81, 114.84) * mm, "mid": v(-319.82, 112.44) * mm, "end": v(-319.05, 109.95) * mm});
            skPoint(sketch, "E525.visualSharp", {"position": v(-314.88, 119.1) * mm});
            skArc(sketch, "E525.filletArc", {"start": v(-312.26, 117.62) * mm, "mid": v(-314.72, 118.06) * mm, "end": v(-316.92, 116.88) * mm});
            skArc(sketch, "E526.filletArc", {"start": v(-295.92, 103.05) * mm, "mid": v(-294.96, 106.23) * mm, "end": v(-296.85, 108.96) * mm});
            skArc(sketch, "E527.filletArc", {"start": v(-308.5, 96.05) * mm, "mid": v(-305.65, 94.55) * mm, "end": v(-302.66, 95.77) * mm});
            skLineSegment(sketch, "E528", {"start": v(-294.24, 133.65) * mm, "end": v(-291.77, 134.94) * mm});
            skLineSegment(sketch, "E529", {"start": v(-287.13, 134.07) * mm, "end": v(-275.5, 120.76) * mm});
            skLineSegment(sketch, "E530", {"start": v(-276.6, 114.88) * mm, "end": v(-285.4, 110.27) * mm});
            skLineSegment(sketch, "E531", {"start": v(-290.8, 112.49) * mm, "end": v(-296.1, 129.11) * mm});
            skPoint(sketch, "E532.visualSharp", {"position": v(-297.07, 132.16) * mm});
            skArc(sketch, "E532.filletArc", {"start": v(-294.24, 133.65) * mm, "mid": v(-296, 131.72) * mm, "end": v(-296.1, 129.11) * mm});
            skPoint(sketch, "E533.visualSharp", {"position": v(-289.1, 136.34) * mm});
            skArc(sketch, "E533.filletArc", {"start": v(-287.13, 134.07) * mm, "mid": v(-289.3, 135.31) * mm, "end": v(-291.77, 134.94) * mm});
            skArc(sketch, "E534.filletArc", {"start": v(-276.6, 114.88) * mm, "mid": v(-274.63, 117.55) * mm, "end": v(-275.5, 120.76) * mm});
            skArc(sketch, "E535.filletArc", {"start": v(-290.8, 112.49) * mm, "mid": v(-288.62, 110.12) * mm, "end": v(-285.4, 110.27) * mm});
            skLineSegment(sketch, "E536", {"start": v(-334.53, 91.14) * mm, "end": v(-333.24, 93.6) * mm});
            skLineSegment(sketch, "E537", {"start": v(-328.93, 95.54) * mm, "end": v(-311.8, 91.22) * mm});
            skLineSegment(sketch, "E538", {"start": v(-309.35, 85.76) * mm, "end": v(-313.94, 76.96) * mm});
            skLineSegment(sketch, "E539", {"start": v(-319.64, 75.7) * mm, "end": v(-333.47, 86.35) * mm});
            skPoint(sketch, "E540.visualSharp", {"position": v(-336, 88.3) * mm});
            skArc(sketch, "E540.filletArc", {"start": v(-334.53, 91.14) * mm, "mid": v(-334.87, 88.55) * mm, "end": v(-333.47, 86.35) * mm});
            skPoint(sketch, "E541.visualSharp", {"position": v(-331.84, 96.27) * mm});
            skArc(sketch, "E541.filletArc", {"start": v(-328.93, 95.54) * mm, "mid": v(-331.42, 95.32) * mm, "end": v(-333.24, 93.6) * mm});
            skArc(sketch, "E542.filletArc", {"start": v(-309.35, 85.76) * mm, "mid": v(-309.25, 89.09) * mm, "end": v(-311.8, 91.22) * mm});
            skArc(sketch, "E543.filletArc", {"start": v(-319.64, 75.7) * mm, "mid": v(-316.5, 75) * mm, "end": v(-313.94, 76.96) * mm});
            skArc(sketch, "E544.MirrorCS", {"start": v(-239.9, 140.54) * mm, "mid": v(-238.38, 142.52) * mm, "end": v(-235.95, 143.13) * mm});
            skLineSegment(sketch, "E545.MirrorCS", {"start": v(-239.9, 140.54) * mm, "end": v(-245.5, 123.77) * mm});
            skArc(sketch, "E546.MirrorCS", {"start": v(-242.21, 118.77) * mm, "mid": v(-245.06, 120.48) * mm, "end": v(-245.5, 123.77) * mm});
            skLineSegment(sketch, "E547.MirrorCS", {"start": v(-242.21, 118.77) * mm, "end": v(-232.32, 117.9) * mm});
            skArc(sketch, "E548.MirrorCS", {"start": v(-228.2, 122.04) * mm, "mid": v(-229.3, 119) * mm, "end": v(-232.32, 117.9) * mm});
            skLineSegment(sketch, "E549.MirrorCS", {"start": v(-228.2, 122.04) * mm, "end": v(-229.72, 139.42) * mm});
            skPoint(sketch, "E550.MirrorP", {"position": v(-230, 142.6) * mm});
            skArc(sketch, "E551.MirrorCS", {"start": v(-208.25, 134.07) * mm, "mid": v(-206.09, 135.31) * mm, "end": v(-203.61, 134.94) * mm});
            skLineSegment(sketch, "E552.MirrorCS", {"start": v(-201.15, 133.65) * mm, "end": v(-203.61, 134.94) * mm});
            skArc(sketch, "E553.MirrorCS", {"start": v(-201.15, 133.65) * mm, "mid": v(-199.4, 131.72) * mm, "end": v(-199.29, 129.11) * mm});
            skLineSegment(sketch, "E554.MirrorCS", {"start": v(-204.59, 112.49) * mm, "end": v(-199.29, 129.11) * mm});
            skLineSegment(sketch, "E555.MirrorCS", {"start": v(-218.78, 114.88) * mm, "end": v(-209.99, 110.27) * mm});
            skArc(sketch, "E556.MirrorCS", {"start": v(-218.78, 114.88) * mm, "mid": v(-220.75, 117.55) * mm, "end": v(-219.88, 120.76) * mm});
            skLineSegment(sketch, "E557.MirrorCS", {"start": v(-208.25, 134.07) * mm, "end": v(-219.88, 120.76) * mm});
            skArc(sketch, "E558.MirrorCS", {"start": v(-233.18, 142.88) * mm, "mid": v(-230.82, 141.78) * mm, "end": v(-229.72, 139.42) * mm});
            skLineSegment(sketch, "E559.MirrorCS", {"start": v(-233.18, 142.88) * mm, "end": v(-235.95, 143.13) * mm});
            skLineSegment(sketch, "E560.MirrorCS", {"start": v(-183.13, 117.62) * mm, "end": v(-198.53, 108.96) * mm});
            skArc(sketch, "E561.MirrorCS", {"start": v(-204.59, 112.49) * mm, "mid": v(-206.77, 110.12) * mm, "end": v(-209.99, 110.27) * mm});
            skArc(sketch, "E562.MirrorCS", {"start": v(-183.13, 117.62) * mm, "mid": v(-180.67, 118.06) * mm, "end": v(-178.46, 116.88) * mm});
            skLineSegment(sketch, "E563.MirrorCS", {"start": v(-176.57, 114.84) * mm, "end": v(-178.46, 116.88) * mm});
            skArc(sketch, "E564.MirrorCS", {"start": v(-176.57, 114.84) * mm, "mid": v(-175.56, 112.44) * mm, "end": v(-176.33, 109.95) * mm});
            skLineSegment(sketch, "E565.MirrorCS", {"start": v(-186.9, 96.05) * mm, "end": v(-176.33, 109.95) * mm});
            skArc(sketch, "E566.MirrorCS", {"start": v(-186.9, 96.05) * mm, "mid": v(-189.74, 94.55) * mm, "end": v(-192.72, 95.77) * mm});
            skLineSegment(sketch, "E567.MirrorCS", {"start": v(-199.46, 103.05) * mm, "end": v(-192.72, 95.77) * mm});
            skArc(sketch, "E568.MirrorCS", {"start": v(-199.46, 103.05) * mm, "mid": v(-200.43, 106.23) * mm, "end": v(-198.53, 108.96) * mm});
            skArc(sketch, "E569.MirrorCS", {"start": v(-160.86, 91.14) * mm, "mid": v(-160.52, 88.55) * mm, "end": v(-161.91, 86.35) * mm});
            skLineSegment(sketch, "E570.MirrorCS", {"start": v(-160.86, 91.14) * mm, "end": v(-162.15, 93.6) * mm});
            skArc(sketch, "E571.MirrorCS", {"start": v(-166.46, 95.54) * mm, "mid": v(-163.97, 95.32) * mm, "end": v(-162.15, 93.6) * mm});
            skLineSegment(sketch, "E572.MirrorCS", {"start": v(-166.46, 95.54) * mm, "end": v(-183.6, 91.22) * mm});
            skArc(sketch, "E573.MirrorCS", {"start": v(-186.04, 85.76) * mm, "mid": v(-186.14, 89.09) * mm, "end": v(-183.6, 91.22) * mm});
            skLineSegment(sketch, "E574.MirrorCS", {"start": v(-186.04, 85.76) * mm, "end": v(-181.44, 76.96) * mm});
            skArc(sketch, "E575.MirrorCS", {"start": v(-175.74, 75.7) * mm, "mid": v(-178.89, 75) * mm, "end": v(-181.44, 76.96) * mm});
            skLineSegment(sketch, "E576.MirrorCS", {"start": v(-175.74, 75.7) * mm, "end": v(-161.91, 86.35) * mm});
            skArc(sketch, "E577.MirrorCS", {"start": v(-157.15, 68.88) * mm, "mid": v(-154.84, 67.92) * mm, "end": v(-153.63, 65.73) * mm});
            skLineSegment(sketch, "E578.MirrorCS", {"start": v(-153.14, 63) * mm, "end": v(-153.63, 65.73) * mm});
            skArc(sketch, "E579.MirrorCS", {"start": v(-153.14, 63) * mm, "mid": v(-153.6, 60.42) * mm, "end": v(-155.6, 58.75) * mm});
            skLineSegment(sketch, "E580.MirrorCS", {"start": v(-157.15, 68.88) * mm, "end": v(-174.79, 69.94) * mm});
            skArc(sketch, "E581.MirrorCS", {"start": v(-178.77, 65.47) * mm, "mid": v(-177.86, 68.67) * mm, "end": v(-174.79, 69.94) * mm});
            skLineSegment(sketch, "E582.MirrorCS", {"start": v(-178.77, 65.47) * mm, "end": v(-177.05, 55.7) * mm});
            skArc(sketch, "E583.MirrorCS", {"start": v(-172, 52.78) * mm, "mid": v(-175.2, 53.06) * mm, "end": v(-177.05, 55.7) * mm});
            skLineSegment(sketch, "E584.MirrorCS", {"start": v(-172, 52.78) * mm, "end": v(-155.6, 58.75) * mm});
            skLineSegment(sketch, "E585.MirrorCS", {"start": v(-323.4, 46.46) * mm, "end": v(-339.8, 40.49) * mm});
            skArc(sketch, "E586.MirrorCS", {"start": v(-323.4, 46.46) * mm, "mid": v(-320.19, 46.17) * mm, "end": v(-318.34, 43.54) * mm});
            skLineSegment(sketch, "E587.MirrorCS", {"start": v(-316.62, 33.76) * mm, "end": v(-318.34, 43.54) * mm});
            skArc(sketch, "E588.MirrorCS", {"start": v(-316.62, 33.76) * mm, "mid": v(-317.52, 30.56) * mm, "end": v(-320.6, 29.3) * mm});
            skLineSegment(sketch, "E589.MirrorCS", {"start": v(-338.24, 30.36) * mm, "end": v(-320.6, 29.3) * mm});
            skArc(sketch, "E590.MirrorCS", {"start": v(-338.24, 30.36) * mm, "mid": v(-340.54, 31.32) * mm, "end": v(-341.76, 33.5) * mm});
            skLineSegment(sketch, "E591.MirrorCS", {"start": v(-342.24, 36.24) * mm, "end": v(-341.76, 33.5) * mm});
            skArc(sketch, "E592.MirrorCS", {"start": v(-342.24, 36.24) * mm, "mid": v(-341.79, 38.81) * mm, "end": v(-339.8, 40.49) * mm});
            skLineSegment(sketch, "E593.MirrorCS", {"start": v(-319.64, 23.53) * mm, "end": v(-333.47, 12.88) * mm});
            skArc(sketch, "E594.MirrorCS", {"start": v(-319.64, 23.53) * mm, "mid": v(-316.5, 24.23) * mm, "end": v(-313.94, 22.27) * mm});
            skLineSegment(sketch, "E595.MirrorCS", {"start": v(-309.35, 13.47) * mm, "end": v(-313.94, 22.27) * mm});
            skArc(sketch, "E596.MirrorCS", {"start": v(-309.35, 13.47) * mm, "mid": v(-309.25, 10.15) * mm, "end": v(-311.8, 8.01) * mm});
            skLineSegment(sketch, "E597.MirrorCS", {"start": v(-328.93, 3.7) * mm, "end": v(-311.8, 8.01) * mm});
            skArc(sketch, "E598.MirrorCS", {"start": v(-328.93, 3.7) * mm, "mid": v(-331.42, 3.92) * mm, "end": v(-333.24, 5.63) * mm});
            skLineSegment(sketch, "E599.MirrorCS", {"start": v(-334.53, 8.1) * mm, "end": v(-333.24, 5.63) * mm});
            skArc(sketch, "E600.MirrorCS", {"start": v(-334.53, 8.1) * mm, "mid": v(-334.87, 10.68) * mm, "end": v(-333.47, 12.88) * mm});
            skArc(sketch, "E601.MirrorCS", {"start": v(-308.5, 3.18) * mm, "mid": v(-305.65, 4.69) * mm, "end": v(-302.66, 3.47) * mm});
            skLineSegment(sketch, "E602.MirrorCS", {"start": v(-308.5, 3.18) * mm, "end": v(-319.05, -10.71) * mm});
            skArc(sketch, "E603.MirrorCS", {"start": v(-318.81, -15.6) * mm, "mid": v(-319.82, -13.2) * mm, "end": v(-319.05, -10.71) * mm});
            skLineSegment(sketch, "E604.MirrorCS", {"start": v(-318.81, -15.6) * mm, "end": v(-316.92, -17.65) * mm});
            skArc(sketch, "E605.MirrorCS", {"start": v(-312.26, -18.38) * mm, "mid": v(-314.72, -18.83) * mm, "end": v(-316.92, -17.65) * mm});
            skLineSegment(sketch, "E606.MirrorCS", {"start": v(-312.26, -18.38) * mm, "end": v(-296.85, -9.73) * mm});
            skArc(sketch, "E607.MirrorCS", {"start": v(-295.92, -3.82) * mm, "mid": v(-294.96, -7) * mm, "end": v(-296.85, -9.73) * mm});
            skLineSegment(sketch, "E608.MirrorCS", {"start": v(-295.92, -3.82) * mm, "end": v(-302.66, 3.47) * mm});
            skArc(sketch, "E609.MirrorCS", {"start": v(-290.8, -13.25) * mm, "mid": v(-288.62, -10.89) * mm, "end": v(-285.4, -11.04) * mm});
            skLineSegment(sketch, "E610.MirrorCS", {"start": v(-290.8, -13.25) * mm, "end": v(-296.1, -29.88) * mm});
            skArc(sketch, "E611.MirrorCS", {"start": v(-294.24, -34.41) * mm, "mid": v(-296, -32.48) * mm, "end": v(-296.1, -29.88) * mm});
            skLineSegment(sketch, "E612.MirrorCS", {"start": v(-294.24, -34.41) * mm, "end": v(-291.77, -35.7) * mm});
            skArc(sketch, "E613.MirrorCS", {"start": v(-287.13, -34.84) * mm, "mid": v(-289.3, -36.08) * mm, "end": v(-291.77, -35.7) * mm});
            skLineSegment(sketch, "E614.MirrorCS", {"start": v(-287.13, -34.84) * mm, "end": v(-275.5, -21.53) * mm});
            skArc(sketch, "E615.MirrorCS", {"start": v(-276.6, -15.65) * mm, "mid": v(-274.63, -18.32) * mm, "end": v(-275.5, -21.53) * mm});
            skLineSegment(sketch, "E616.MirrorCS", {"start": v(-276.6, -15.65) * mm, "end": v(-285.4, -11.04) * mm});
            skArc(sketch, "E617.MirrorCS", {"start": v(-267.2, -22.8) * mm, "mid": v(-266.09, -19.77) * mm, "end": v(-263.06, -18.67) * mm});
            skLineSegment(sketch, "E618.MirrorCS", {"start": v(-253.17, -19.54) * mm, "end": v(-263.06, -18.67) * mm});
            skArc(sketch, "E619.MirrorCS", {"start": v(-253.17, -19.54) * mm, "mid": v(-250.32, -21.24) * mm, "end": v(-249.9, -24.54) * mm});
            skLineSegment(sketch, "E620.MirrorCS", {"start": v(-255.48, -41.3) * mm, "end": v(-249.9, -24.54) * mm});
            skPoint(sketch, "E621.MirrorP", {"position": v(-256.44, -44.15) * mm});
            skArc(sketch, "E622.MirrorCS", {"start": v(-255.48, -41.3) * mm, "mid": v(-257, -43.28) * mm, "end": v(-259.43, -43.9) * mm});
            skLineSegment(sketch, "E623.MirrorCS", {"start": v(-262.2, -43.65) * mm, "end": v(-259.43, -43.9) * mm});
            skArc(sketch, "E624.MirrorCS", {"start": v(-262.2, -43.65) * mm, "mid": v(-264.57, -42.55) * mm, "end": v(-265.67, -40.18) * mm});
            skLineSegment(sketch, "E625.MirrorCS", {"start": v(-267.2, -22.8) * mm, "end": v(-265.67, -40.18) * mm});
            skArc(sketch, "E626.MirrorCS", {"start": v(-242.21, -19.54) * mm, "mid": v(-245.06, -21.24) * mm, "end": v(-245.5, -24.54) * mm});
            skLineSegment(sketch, "E627.MirrorCS", {"start": v(-242.21, -19.54) * mm, "end": v(-232.32, -18.67) * mm});
            skArc(sketch, "E628.MirrorCS", {"start": v(-228.2, -22.8) * mm, "mid": v(-229.3, -19.77) * mm, "end": v(-232.32, -18.67) * mm});
            skLineSegment(sketch, "E629.MirrorCS", {"start": v(-228.2, -22.8) * mm, "end": v(-229.72, -40.18) * mm});
            skArc(sketch, "E630.MirrorCS", {"start": v(-233.18, -43.65) * mm, "mid": v(-230.82, -42.55) * mm, "end": v(-229.72, -40.18) * mm});
            skLineSegment(sketch, "E631.MirrorCS", {"start": v(-233.18, -43.65) * mm, "end": v(-235.95, -43.9) * mm});
            skArc(sketch, "E632.MirrorCS", {"start": v(-239.9, -41.3) * mm, "mid": v(-238.38, -43.28) * mm, "end": v(-235.95, -43.9) * mm});
            skLineSegment(sketch, "E633.MirrorCS", {"start": v(-239.9, -41.3) * mm, "end": v(-245.5, -24.54) * mm});
            skArc(sketch, "E634.MirrorCS", {"start": v(-218.78, -15.65) * mm, "mid": v(-220.75, -18.32) * mm, "end": v(-219.88, -21.53) * mm});
            skLineSegment(sketch, "E635.MirrorCS", {"start": v(-218.78, -15.65) * mm, "end": v(-209.99, -11.04) * mm});
            skArc(sketch, "E636.MirrorCS", {"start": v(-204.59, -13.25) * mm, "mid": v(-206.77, -10.89) * mm, "end": v(-209.99, -11.04) * mm});
            skArc(sketch, "E637.MirrorCS", {"start": v(-201.15, -34.41) * mm, "mid": v(-199.4, -32.48) * mm, "end": v(-199.29, -29.88) * mm});
            skLineSegment(sketch, "E638.MirrorCS", {"start": v(-201.15, -34.41) * mm, "end": v(-203.61, -35.7) * mm});
            skArc(sketch, "E639.MirrorCS", {"start": v(-208.25, -34.84) * mm, "mid": v(-206.09, -36.08) * mm, "end": v(-203.61, -35.7) * mm});
            skLineSegment(sketch, "E640.MirrorCS", {"start": v(-208.25, -34.84) * mm, "end": v(-219.88, -21.53) * mm});
            skLineSegment(sketch, "E641.MirrorCS", {"start": v(-199.46, -3.82) * mm, "end": v(-192.72, 3.47) * mm});
            skArc(sketch, "E642.MirrorCS", {"start": v(-199.46, -3.82) * mm, "mid": v(-200.43, -7) * mm, "end": v(-198.53, -9.73) * mm});
            skArc(sketch, "E643.MirrorCS", {"start": v(-183.13, -18.38) * mm, "mid": v(-180.67, -18.83) * mm, "end": v(-178.46, -17.65) * mm});
            skLineSegment(sketch, "E644.MirrorCS", {"start": v(-176.57, -15.6) * mm, "end": v(-178.46, -17.65) * mm});
            skArc(sketch, "E645.MirrorCS", {"start": v(-176.57, -15.6) * mm, "mid": v(-175.56, -13.2) * mm, "end": v(-176.33, -10.71) * mm});
            skLineSegment(sketch, "E646.MirrorCS", {"start": v(-186.9, 3.18) * mm, "end": v(-176.33, -10.71) * mm});
            skArc(sketch, "E647.MirrorCS", {"start": v(-186.04, 13.47) * mm, "mid": v(-186.14, 10.15) * mm, "end": v(-183.6, 8.01) * mm});
            skLineSegment(sketch, "E648.MirrorCS", {"start": v(-186.04, 13.47) * mm, "end": v(-181.44, 22.27) * mm});
            skArc(sketch, "E649.MirrorCS", {"start": v(-175.74, 23.53) * mm, "mid": v(-178.89, 24.23) * mm, "end": v(-181.44, 22.27) * mm});
            skLineSegment(sketch, "E650.MirrorCS", {"start": v(-175.74, 23.53) * mm, "end": v(-161.91, 12.88) * mm});
            skLineSegment(sketch, "E651.MirrorCS", {"start": v(-166.46, 3.7) * mm, "end": v(-183.6, 8.01) * mm});
            skArc(sketch, "E652.MirrorCS", {"start": v(-166.46, 3.7) * mm, "mid": v(-163.97, 3.92) * mm, "end": v(-162.15, 5.63) * mm});
            skLineSegment(sketch, "E653.MirrorCS", {"start": v(-160.86, 8.1) * mm, "end": v(-162.15, 5.63) * mm});
            skArc(sketch, "E654.MirrorCS", {"start": v(-160.86, 8.1) * mm, "mid": v(-160.52, 10.68) * mm, "end": v(-161.91, 12.88) * mm});
            skLineSegment(sketch, "E655.MirrorCS", {"start": v(-157.15, 30.36) * mm, "end": v(-174.79, 29.3) * mm});
            skArc(sketch, "E656.MirrorCS", {"start": v(-178.77, 33.76) * mm, "mid": v(-177.86, 30.56) * mm, "end": v(-174.79, 29.3) * mm});
            skLineSegment(sketch, "E657.MirrorCS", {"start": v(-178.77, 33.76) * mm, "end": v(-177.05, 43.54) * mm});
            skArc(sketch, "E658.MirrorCS", {"start": v(-172, 46.46) * mm, "mid": v(-175.2, 46.17) * mm, "end": v(-177.05, 43.54) * mm});
            skLineSegment(sketch, "E659.MirrorCS", {"start": v(-172, 46.46) * mm, "end": v(-155.6, 40.49) * mm});
            skArc(sketch, "E660.MirrorCS", {"start": v(-153.14, 36.24) * mm, "mid": v(-153.6, 38.81) * mm, "end": v(-155.6, 40.49) * mm});
            skLineSegment(sketch, "E661.MirrorCS", {"start": v(-153.14, 36.24) * mm, "end": v(-153.63, 33.5) * mm});
            skArc(sketch, "E662.MirrorCS", {"start": v(-157.15, 30.36) * mm, "mid": v(-154.84, 31.32) * mm, "end": v(-153.63, 33.5) * mm});
            skLineSegment(sketch, "E663.MirrorCS", {"start": v(-204.59, -13.25) * mm, "end": v(-199.29, -29.88) * mm});
            skArc(sketch, "E664.MirrorCS", {"start": v(-186.9, 3.18) * mm, "mid": v(-189.74, 4.69) * mm, "end": v(-192.72, 3.47) * mm});
            skLineSegment(sketch, "E665.MirrorCS", {"start": v(-183.13, -18.38) * mm, "end": v(-198.53, -9.73) * mm});
            skSolve(sketch);
        }
        {
            var Q0;
            Q0=qSketchRegion(id+"F2",true);
            extrude(context, id + "F3", {"entities" : qUnion([Q0]), "depth" : 6.35 * mm});
        }
    });
